# Revit family: 879-003X99-001-DN65-250
name_source: partatom
category: Pipe Accessories
units: mm (PartAtom-declared; Revit-internal decimal feet)

## family parameters
Always vertical = Yes
Cut with Voids When Loaded = No
Part Type = Valve - Breaks Into
Round Connector Dimension = Use Diameter
Shared = No
Work Plane-Based = No

## types (47) — shared parameters
879-0065-00-14400309999 = DN65_PN10/16
879-0065-00-14400319999 = DN65_PN10/16
879-0065-00-144003199A0 = DN65_PN10/16
879-0065-00-14400329999 = DN65_PN10/16
879-0065-00-14400339999 = DN65_PN10/16
879-0080-00-14400309999 = DN80_PN10/16
879-0080-00-14400319999 = DN80_PN10/16
879-0080-00-144003199A0 = DN80_PN10/16
879-0080-00-14400329999 = DN80_PN10/16
879-0080-00-14400339999 = DN80_PN10/16
879-0100-00-14400309999 = DN100_PN10/16
879-0100-00-14400319999 = DN100_PN10/16
879-0100-00-144003199A0 = DN100_PN10/16
879-0100-00-14400329999 = DN100_PN10/16
879-0100-00-14400339999 = DN100_PN10/16
879-0125-00-14400309999 = DN125_PN10/16
879-0125-00-14400319999 = DN125_PN10/16
879-0125-00-144003199A0 = DN125_PN10/16
879-0125-00-14400329999 = DN125_PN10/16
879-0125-00-14400339999 = DN125_PN10/16
879-0150-00-14400309999 = DN150_PN10/16
879-0150-00-14400319999 = DN150_PN10/16
879-0150-00-144003199A0 = DN150_PN10/16
879-0150-00-14400329999 = DN150_PN10/16
879-0150-00-14400339999 = DN150_PN10/16
879-0200-00-04400309999 = DN200_PN10
879-0200-00-04400319999 = DN200_PN10
879-0200-00-044003199A0 = DN200_PN10
879-0200-00-04400329999 = DN200_PN10
879-0200-00-04400339999 = DN200_PN10
879-0200-00-14400309999 = DN200_PN16
879-0200-00-14400319999 = DN200_PN16
879-0200-00-144003199A0 = DN200_PN16
879-0200-00-14400329999 = DN200_PN16
879-0200-00-14400339999 = DN200_PN16
879-0250-00-04400309999 = DN250_PN10
879-0250-00-04400319999 = DN250_PN10
879-0250-00-044003199A0 = DN250_PN10
879-0250-00-04400329999 = DN250_PN10
879-0250-00-04400339999 = DN250_PN10
879-0250-00-14400309999 = DN250_PN16
879-0250-00-14400319999 = DN250_PN16
879-0250-00-144003199A0 = DN250_PN16
879-0250-00-14400329999 = DN250_PN16
879-0250-00-14400339999 = DN250_PN16
Body_wall_thickness = 10 mm  [stored 0.0328084 ft]
Description_ = AVK ONE WAY ALTITUDE LEVEL CONTROL VALVE
Search_Table = 879-003X99-001-DN65-250
URL product pages = https://www.avkvalves.com

## per-type parameters (varying)
- 879-0065-00-14400309999_DN65_PN10/16: Body_Collar_Dia=26 mm; Body_Collar_Dia_2=18 mm  [stored 0.0590551 ft]; Body_Flange_Dia=83 mm; Body_Flange_Dia_2=91 mm; Body_Height_1=73 mm; Body_Height_2=36 mm; Body_Height_3=58 mm; Body_Height_4=51 mm; Body_Top_Dia=11 mm  [stored 0.0360892 ft]; Body_Top_Dia_2=9 mm  [stored 0.0295276 ft]; Body_With_Dia=36 mm; Body_With_Dia_1=73 mm; Body_With_Dia_2=73 mm; Bolt_support=223 mm; Bolt_support_2=112 mm; Bolt_support_Dia=12 mm  [stored 0.0393701 ft]; Bolt_support_lenght=53 mm; Bolt_support_lenght_2=63 mm; Bottom_profile=16 mm  [stored 0.0524934 ft]; D1=59 mm; D3=93 mm; DN=65 mm; Fillet_Length=6 mm  [stored 0.019685 ft]; Fillet_Length_Ref=18 mm  [stored 0.0590551 ft]; Flange_thickness=19 mm  [stored 0.062336 ft]; H=540 mm; H3_Ref=534 mm; ID=33 mm; L=290 mm; L_Ref=126 mm; NV_Dia=65 mm; PG_Dia=33 mm; PG_Ref=48 mm; PG_depth=8 mm  [stored 0.0262467 ft]; PG_height=232 mm; PG_height_1=216 mm; PG_ref=43 mm  [stored 0.141076 ft]; PR_1=71 mm; P_lenght=39 mm  [stored 0.127953 ft]; Pilot_Dia_1=18 mm  [stored 0.0590551 ft]; Pilot_Dia_2=35 mm  [stored 0.114829 ft]; Pilot_Dia_3=12 mm  [stored 0.0393701 ft]; Pilot_Dia_4=6 mm  [stored 0.019685 ft]; Pilot_Dia_5=4 mm  [stored 0.0131234 ft]; Pilot_top_1=312 mm; Pilot_top_ref=120 mm; Profile1_Height=117 mm; Profile1_Length=25 mm  [stored 0.082021 ft]; Profile1_Length_2=17 mm; Profile_Dia=6 mm  [stored 0.019685 ft]; Profile_Dia_2=6 mm  [stored 0.019685 ft]; Profile_Dia_3=12 mm  [stored 0.0393701 ft]; Profile_Dia_Ref=3 mm  [stored 0.00984252 ft]; Profile_Dia_Ref_2=12 mm  [stored 0.0393701 ft]; Profile_height ref=12 mm  [stored 0.0393701 ft]; T_Height=313 mm; T_Height_2=268 mm; T_Height_Ref_1=45 mm; T_Height_Ref_2=52 mm; T_ref=270 mm; Top_Profile=134 mm; Top_Profile_Ref=139 mm; W=540 mm; W_Ref=532 mm
- 879-0065-00-14400319999_DN65_PN10/16: Body_Collar_Dia=26 mm; Body_Collar_Dia_2=18 mm  [stored 0.0590551 ft]; Body_Flange_Dia=83 mm; Body_Flange_Dia_2=91 mm; Body_Height_1=73 mm; Body_Height_2=36 mm; Body_Height_3=58 mm; Body_Height_4=51 mm; Body_Top_Dia=11 mm  [stored 0.0360892 ft]; Body_Top_Dia_2=9 mm  [stored 0.0295276 ft]; Body_With_Dia=36 mm; Body_With_Dia_1=73 mm; Body_With_Dia_2=73 mm; Bolt_support=223 mm; Bolt_support_2=112 mm; Bolt_support_Dia=12 mm  [stored 0.0393701 ft]; Bolt_support_lenght=53 mm; Bolt_support_lenght_2=63 mm; Bottom_profile=16 mm  [stored 0.0524934 ft]; D1=59 mm; D3=93 mm; DN=65 mm; Fillet_Length=6 mm  [stored 0.019685 ft]; Fillet_Length_Ref=18 mm  [stored 0.0590551 ft]; Flange_thickness=19 mm  [stored 0.062336 ft]; H=540 mm; H3_Ref=534 mm; ID=33 mm; L=290 mm; L_Ref=126 mm; NV_Dia=65 mm; PG_Dia=33 mm; PG_Ref=48 mm; PG_depth=8 mm  [stored 0.0262467 ft]; PG_height=246 mm; PG_height_1=230 mm; PG_ref=43 mm  [stored 0.141076 ft]; PR_1=67 mm; P_lenght=39 mm  [stored 0.127953 ft]; Pilot_Dia_1=18 mm  [stored 0.0590551 ft]; Pilot_Dia_2=35 mm  [stored 0.114829 ft]; Pilot_Dia_3=12 mm  [stored 0.0393701 ft]; Pilot_Dia_4=6 mm  [stored 0.019685 ft]; Pilot_Dia_5=4 mm  [stored 0.0131234 ft]; Pilot_top_1=312 mm; Pilot_top_ref=120 mm; Profile1_Height=135 mm; Profile1_Length=25 mm  [stored 0.082021 ft]; Profile1_Length_2=17 mm; Profile_Dia=6 mm  [stored 0.019685 ft]; Profile_Dia_2=6 mm  [stored 0.019685 ft]; Profile_Dia_3=12 mm  [stored 0.0393701 ft]; Profile_Dia_Ref=3 mm  [stored 0.00984252 ft]; Profile_Dia_Ref_2=12 mm  [stored 0.0393701 ft]; Profile_height ref=12 mm  [stored 0.0393701 ft]; T_Height=295 mm; T_Height_2=252 mm; T_Height_Ref_1=42 mm; T_Height_Ref_2=49 mm; T_ref=280 mm; Top_Profile=134 mm; Top_Profile_Ref=139 mm; W=540 mm; W_Ref=532 mm
- 879-0065-00-144003199A0_DN65_PN10/16: Body_Collar_Dia=26 mm; Body_Collar_Dia_2=18 mm  [stored 0.0590551 ft]; Body_Flange_Dia=83 mm; Body_Flange_Dia_2=91 mm; Body_Height_1=73 mm; Body_Height_2=36 mm; Body_Height_3=58 mm; Body_Height_4=51 mm; Body_Top_Dia=11 mm  [stored 0.0360892 ft]; Body_Top_Dia_2=9 mm  [stored 0.0295276 ft]; Body_With_Dia=36 mm; Body_With_Dia_1=73 mm; Body_With_Dia_2=73 mm; Bolt_support=223 mm; Bolt_support_2=112 mm; Bolt_support_Dia=12 mm  [stored 0.0393701 ft]; Bolt_support_lenght=53 mm; Bolt_support_lenght_2=63 mm; Bottom_profile=16 mm  [stored 0.0524934 ft]; D1=59 mm; D3=93 mm; DN=65 mm; Fillet_Length=6 mm  [stored 0.019685 ft]; Fillet_Length_Ref=18 mm  [stored 0.0590551 ft]; Flange_thickness=19 mm  [stored 0.062336 ft]; H=540 mm; H3_Ref=534 mm; ID=33 mm; L=290 mm; L_Ref=126 mm; NV_Dia=65 mm; PG_Dia=33 mm; PG_Ref=48 mm; PG_depth=8 mm  [stored 0.0262467 ft]; PG_height=232 mm; PG_height_1=216 mm; PG_ref=43 mm  [stored 0.141076 ft]; PR_1=71 mm; P_lenght=39 mm  [stored 0.127953 ft]; Pilot_Dia_1=18 mm  [stored 0.0590551 ft]; Pilot_Dia_2=35 mm  [stored 0.114829 ft]; Pilot_Dia_3=12 mm  [stored 0.0393701 ft]; Pilot_Dia_4=6 mm  [stored 0.019685 ft]; Pilot_Dia_5=4 mm  [stored 0.0131234 ft]; Pilot_top_1=312 mm; Pilot_top_ref=120 mm; Profile1_Height=117 mm; Profile1_Length=25 mm  [stored 0.082021 ft]; Profile1_Length_2=17 mm; Profile_Dia=6 mm  [stored 0.019685 ft]; Profile_Dia_2=6 mm  [stored 0.019685 ft]; Profile_Dia_3=12 mm  [stored 0.0393701 ft]; Profile_Dia_Ref=3 mm  [stored 0.00984252 ft]; Profile_Dia_Ref_2=12 mm  [stored 0.0393701 ft]; Profile_height ref=12 mm  [stored 0.0393701 ft]; T_Height=313 mm; T_Height_2=268 mm; T_Height_Ref_1=45 mm; T_Height_Ref_2=52 mm; T_ref=270 mm; Top_Profile=134 mm; Top_Profile_Ref=139 mm; W=540 mm; W_Ref=532 mm
- 879-0065-00-14400329999_DN65_PN10/16: Body_Collar_Dia=26 mm; Body_Collar_Dia_2=18 mm  [stored 0.0590551 ft]; Body_Flange_Dia=83 mm; Body_Flange_Dia_2=91 mm; Body_Height_1=73 mm; Body_Height_2=36 mm; Body_Height_3=73 mm; Body_Height_4=51 mm; Body_Top_Dia=11 mm  [stored 0.0360892 ft]; Body_Top_Dia_2=9 mm  [stored 0.0295276 ft]; Body_With_Dia=36 mm; Body_With_Dia_1=73 mm; Body_With_Dia_2=73 mm; Bolt_support=223 mm; Bolt_support_2=112 mm; Bolt_support_Dia=12 mm  [stored 0.0393701 ft]; Bolt_support_lenght=53 mm; Bolt_support_lenght_2=63 mm; Bottom_profile=16 mm  [stored 0.0524934 ft]; D1=59 mm; D3=93 mm; DN=65 mm; Fillet_Length=6 mm  [stored 0.019685 ft]; Fillet_Length_Ref=18 mm  [stored 0.0590551 ft]; Flange_thickness=19 mm  [stored 0.062336 ft]; H=540 mm; H3_Ref=534 mm; ID=33 mm; L=290 mm; L_Ref=126 mm; NV_Dia=65 mm; PG_Dia=33 mm; PG_Ref=48 mm; PG_depth=8 mm  [stored 0.0262467 ft]; PG_height=246 mm; PG_height_1=230 mm; PG_ref=43 mm  [stored 0.141076 ft]; PR_1=67 mm; P_lenght=39 mm  [stored 0.127953 ft]; Pilot_Dia_1=18 mm  [stored 0.0590551 ft]; Pilot_Dia_2=35 mm  [stored 0.114829 ft]; Pilot_Dia_3=12 mm  [stored 0.0393701 ft]; Pilot_Dia_4=6 mm  [stored 0.019685 ft]; Pilot_Dia_5=4 mm  [stored 0.0131234 ft]; Pilot_top_1=319 mm; Pilot_top_ref=113 mm; Profile1_Height=135 mm; Profile1_Length=25 mm  [stored 0.082021 ft]; Profile1_Length_2=17 mm; Profile_Dia=6 mm  [stored 0.019685 ft]; Profile_Dia_2=6 mm  [stored 0.019685 ft]; Profile_Dia_3=12 mm  [stored 0.0393701 ft]; Profile_Dia_Ref=3 mm  [stored 0.00984252 ft]; Profile_Dia_Ref_2=12 mm  [stored 0.0393701 ft]; Profile_height ref=12 mm  [stored 0.0393701 ft]; T_Height=295 mm; T_Height_2=252 mm; T_Height_Ref_1=42 mm; T_Height_Ref_2=49 mm; T_ref=280 mm; Top_Profile=134 mm; Top_Profile_Ref=139 mm; W=540 mm; W_Ref=532 mm
- 879-0065-00-14400339999_DN65_PN10/16: Body_Collar_Dia=26 mm; Body_Collar_Dia_2=18 mm  [stored 0.0590551 ft]; Body_Flange_Dia=83 mm; Body_Flange_Dia_2=91 mm; Body_Height_1=73 mm; Body_Height_2=36 mm; Body_Height_3=58 mm; Body_Height_4=51 mm; Body_Top_Dia=11 mm  [stored 0.0360892 ft]; Body_Top_Dia_2=9 mm  [stored 0.0295276 ft]; Body_With_Dia=36 mm; Body_With_Dia_1=73 mm; Body_With_Dia_2=73 mm; Bolt_support=223 mm; Bolt_support_2=112 mm; Bolt_support_Dia=12 mm  [stored 0.0393701 ft]; Bolt_support_lenght=53 mm; Bolt_support_lenght_2=63 mm; Bottom_profile=16 mm  [stored 0.0524934 ft]; D1=59 mm; D3=93 mm; DN=65 mm; Fillet_Length=6 mm  [stored 0.019685 ft]; Fillet_Length_Ref=18 mm  [stored 0.0590551 ft]; Flange_thickness=19 mm  [stored 0.062336 ft]; H=540 mm; H3_Ref=534 mm; ID=33 mm; L=290 mm; L_Ref=126 mm; NV_Dia=65 mm; PG_Dia=33 mm; PG_Ref=48 mm; PG_depth=8 mm  [stored 0.0262467 ft]; PG_height=232 mm; PG_height_1=216 mm; PG_ref=43 mm  [stored 0.141076 ft]; PR_1=71 mm; P_lenght=39 mm  [stored 0.127953 ft]; Pilot_Dia_1=18 mm  [stored 0.0590551 ft]; Pilot_Dia_2=35 mm  [stored 0.114829 ft]; Pilot_Dia_3=12 mm  [stored 0.0393701 ft]; Pilot_Dia_4=6 mm  [stored 0.019685 ft]; Pilot_Dia_5=4 mm  [stored 0.0131234 ft]; Pilot_top_1=312 mm; Pilot_top_ref=120 mm; Profile1_Height=117 mm; Profile1_Length=25 mm  [stored 0.082021 ft]; Profile1_Length_2=17 mm; Profile_Dia=6 mm  [stored 0.019685 ft]; Profile_Dia_2=6 mm  [stored 0.019685 ft]; Profile_Dia_3=12 mm  [stored 0.0393701 ft]; Profile_Dia_Ref=3 mm  [stored 0.00984252 ft]; Profile_Dia_Ref_2=12 mm  [stored 0.0393701 ft]; Profile_height ref=12 mm  [stored 0.0393701 ft]; T_Height=313 mm; T_Height_2=268 mm; T_Height_Ref_1=45 mm; T_Height_Ref_2=52 mm; T_ref=270 mm; Top_Profile=134 mm; Top_Profile_Ref=139 mm; W=540 mm; W_Ref=532 mm
- 879-0080-00-14400309999_DN80_PN10/16: Body_Collar_Dia=28 mm; Body_Collar_Dia_2=19 mm  [stored 0.062336 ft]; Body_Flange_Dia=89 mm; Body_Flange_Dia_2=97 mm; Body_Height_1=78 mm; Body_Height_2=39 mm  [stored 0.127953 ft]; Body_Height_3=62 mm; Body_Height_4=54 mm; Body_Top_Dia=11 mm  [stored 0.0360892 ft]; Body_Top_Dia_2=10 mm  [stored 0.0328084 ft]; Body_With_Dia=39 mm  [stored 0.127953 ft]; Body_With_Dia_1=78 mm; Body_With_Dia_2=78 mm; Bolt_support=238 mm; Bolt_support_2=119 mm; Bolt_support_Dia=12 mm  [stored 0.0393701 ft]; Bolt_support_lenght=60 mm; Bolt_support_lenght_2=70 mm; Bottom_profile=20 mm  [stored 0.0656168 ft]; D1=66 mm; D3=100 mm; DN=80 mm; Fillet_Length=6 mm  [stored 0.019685 ft]; Fillet_Length_Ref=18 mm  [stored 0.0590551 ft]; Flange_thickness=19 mm  [stored 0.062336 ft]; H=555 mm; H3_Ref=549 mm; ID=40 mm  [stored 0.131234 ft]; L=310 mm; L_Ref=136 mm; NV_Dia=80 mm; PG_Dia=40 mm  [stored 0.131234 ft]; PG_Ref=52 mm; PG_depth=8 mm  [stored 0.0262467 ft]; PG_height=262 mm; PG_height_1=242 mm; PG_ref=50 mm; PR_1=66 mm; P_lenght=43 mm  [stored 0.141076 ft]; Pilot_Dia_1=20 mm  [stored 0.0656168 ft]; Pilot_Dia_2=39 mm  [stored 0.127953 ft]; Pilot_Dia_3=13 mm; Pilot_Dia_4=7 mm  [stored 0.0229659 ft]; Pilot_Dia_5=4 mm  [stored 0.0131234 ft]; Pilot_top_1=321 mm; Pilot_top_ref=118 mm; Profile1_Height=144 mm; Profile1_Length=27 mm  [stored 0.0885827 ft]; Profile1_Length_2=18 mm  [stored 0.0590551 ft]; Profile_Dia=6 mm  [stored 0.019685 ft]; Profile_Dia_2=6 mm  [stored 0.019685 ft]; Profile_Dia_3=12 mm  [stored 0.0393701 ft]; Profile_Dia_Ref=3 mm  [stored 0.00984252 ft]; Profile_Dia_Ref_2=12 mm  [stored 0.0393701 ft]; Profile_height ref=12 mm  [stored 0.0393701 ft]; T_Height=293 mm; T_Height_2=251 mm; T_Height_Ref_1=42 mm; T_Height_Ref_2=49 mm; T_ref=289 mm; Top_Profile=143 mm; Top_Profile_Ref=148 mm; W=560 mm; W_Ref=552 mm
- 879-0080-00-144003099A0_DN80_PN10/16: Body_Collar_Dia=28 mm; Body_Collar_Dia_2=19 mm  [stored 0.062336 ft]; Body_Flange_Dia=89 mm; Body_Flange_Dia_2=97 mm; Body_Height_1=78 mm; Body_Height_2=39 mm  [stored 0.127953 ft]; Body_Height_3=62 mm; Body_Height_4=54 mm; Body_Top_Dia=11 mm  [stored 0.0360892 ft]; Body_Top_Dia_2=10 mm  [stored 0.0328084 ft]; Body_With_Dia=39 mm  [stored 0.127953 ft]; Body_With_Dia_1=78 mm; Body_With_Dia_2=78 mm; Bolt_support=238 mm; Bolt_support_2=119 mm; Bolt_support_Dia=12 mm  [stored 0.0393701 ft]; Bolt_support_lenght=60 mm; Bolt_support_lenght_2=70 mm; Bottom_profile=20 mm  [stored 0.0656168 ft]; D1=66 mm; D3=100 mm; DN=80 mm; Fillet_Length=6 mm  [stored 0.019685 ft]; Fillet_Length_Ref=18 mm  [stored 0.0590551 ft]; Flange_thickness=19 mm  [stored 0.062336 ft]; H=555 mm; H3_Ref=549 mm; ID=40 mm  [stored 0.131234 ft]; L=310 mm; L_Ref=136 mm; NV_Dia=80 mm; PG_Dia=40 mm  [stored 0.131234 ft]; PG_Ref=52 mm; PG_depth=8 mm  [stored 0.0262467 ft]; PG_height=254 mm; PG_height_1=234 mm; PG_ref=50 mm; PR_1=69 mm; P_lenght=43 mm  [stored 0.141076 ft]; Pilot_Dia_1=20 mm  [stored 0.0656168 ft]; Pilot_Dia_2=39 mm  [stored 0.127953 ft]; Pilot_Dia_3=13 mm; Pilot_Dia_4=7 mm  [stored 0.0229659 ft]; Pilot_Dia_5=4 mm  [stored 0.0131234 ft]; Pilot_top_1=321 mm; Pilot_top_ref=118 mm; Profile1_Height=133 mm; Profile1_Length=27 mm  [stored 0.0885827 ft]; Profile1_Length_2=18 mm  [stored 0.0590551 ft]; Profile_Dia=6 mm  [stored 0.019685 ft]; Profile_Dia_2=6 mm  [stored 0.019685 ft]; Profile_Dia_3=12 mm  [stored 0.0393701 ft]; Profile_Dia_Ref=3 mm  [stored 0.00984252 ft]; Profile_Dia_Ref_2=12 mm  [stored 0.0393701 ft]; Profile_height ref=12 mm  [stored 0.0393701 ft]; T_Height=304 mm; T_Height_2=261 mm; T_Height_Ref_1=43 mm  [stored 0.141076 ft]; T_Height_Ref_2=51 mm; T_ref=283 mm; Top_Profile=143 mm; Top_Profile_Ref=148 mm; W=560 mm; W_Ref=552 mm
- 879-0080-00-14400319999_DN80_PN10/16: Body_Collar_Dia=28 mm; Body_Collar_Dia_2=19 mm  [stored 0.062336 ft]; Body_Flange_Dia=89 mm; Body_Flange_Dia_2=97 mm; Body_Height_1=78 mm; Body_Height_2=39 mm  [stored 0.127953 ft]; Body_Height_3=62 mm; Body_Height_4=54 mm; Body_Top_Dia=11 mm  [stored 0.0360892 ft]; Body_Top_Dia_2=10 mm  [stored 0.0328084 ft]; Body_With_Dia=39 mm  [stored 0.127953 ft]; Body_With_Dia_1=78 mm; Body_With_Dia_2=78 mm; Bolt_support=238 mm; Bolt_support_2=119 mm; Bolt_support_Dia=12 mm  [stored 0.0393701 ft]; Bolt_support_lenght=60 mm; Bolt_support_lenght_2=70 mm; Bottom_profile=20 mm  [stored 0.0656168 ft]; D1=66 mm; D3=100 mm; DN=80 mm; Fillet_Length=6 mm  [stored 0.019685 ft]; Fillet_Length_Ref=18 mm  [stored 0.0590551 ft]; Flange_thickness=19 mm  [stored 0.062336 ft]; H=555 mm; H3_Ref=549 mm; ID=40 mm  [stored 0.131234 ft]; L=310 mm; L_Ref=136 mm; NV_Dia=80 mm; PG_Dia=40 mm  [stored 0.131234 ft]; PG_Ref=52 mm; PG_depth=8 mm  [stored 0.0262467 ft]; PG_height=262 mm; PG_height_1=242 mm; PG_ref=50 mm; PR_1=66 mm; P_lenght=43 mm  [stored 0.141076 ft]; Pilot_Dia_1=20 mm  [stored 0.0656168 ft]; Pilot_Dia_2=39 mm  [stored 0.127953 ft]; Pilot_Dia_3=13 mm; Pilot_Dia_4=7 mm  [stored 0.0229659 ft]; Pilot_Dia_5=4 mm  [stored 0.0131234 ft]; Pilot_top_1=321 mm; Pilot_top_ref=118 mm; Profile1_Height=144 mm; Profile1_Length=27 mm  [stored 0.0885827 ft]; Profile1_Length_2=18 mm  [stored 0.0590551 ft]; Profile_Dia=6 mm  [stored 0.019685 ft]; Profile_Dia_2=6 mm  [stored 0.019685 ft]; Profile_Dia_3=12 mm  [stored 0.0393701 ft]; Profile_Dia_Ref=3 mm  [stored 0.00984252 ft]; Profile_Dia_Ref_2=12 mm  [stored 0.0393701 ft]; Profile_height ref=12 mm  [stored 0.0393701 ft]; T_Height=293 mm; T_Height_2=251 mm; T_Height_Ref_1=42 mm; T_Height_Ref_2=49 mm; T_ref=289 mm; Top_Profile=143 mm; Top_Profile_Ref=148 mm; W=560 mm; W_Ref=552 mm
- 879-0080-00-144003199A0_DN80_PN10/16: Body_Collar_Dia=28 mm; Body_Collar_Dia_2=19 mm  [stored 0.062336 ft]; Body_Flange_Dia=89 mm; Body_Flange_Dia_2=97 mm; Body_Height_1=78 mm; Body_Height_2=39 mm  [stored 0.127953 ft]; Body_Height_3=78 mm; Body_Height_4=54 mm; Body_Top_Dia=11 mm  [stored 0.0360892 ft]; Body_Top_Dia_2=10 mm  [stored 0.0328084 ft]; Body_With_Dia=39 mm  [stored 0.127953 ft]; Body_With_Dia_1=78 mm; Body_With_Dia_2=78 mm; Bolt_support=238 mm; Bolt_support_2=119 mm; Bolt_support_Dia=12 mm  [stored 0.0393701 ft]; Bolt_support_lenght=60 mm; Bolt_support_lenght_2=70 mm; Bottom_profile=20 mm  [stored 0.0656168 ft]; D1=66 mm; D3=100 mm; DN=80 mm; Fillet_Length=6 mm  [stored 0.019685 ft]; Fillet_Length_Ref=18 mm  [stored 0.0590551 ft]; Flange_thickness=19 mm  [stored 0.062336 ft]; H=555 mm; H3_Ref=549 mm; ID=40 mm  [stored 0.131234 ft]; L=310 mm; L_Ref=136 mm; NV_Dia=80 mm; PG_Dia=40 mm  [stored 0.131234 ft]; PG_Ref=52 mm; PG_depth=8 mm  [stored 0.0262467 ft]; PG_height=254 mm; PG_height_1=234 mm; PG_ref=50 mm; PR_1=69 mm; P_lenght=43 mm  [stored 0.141076 ft]; Pilot_Dia_1=20 mm  [stored 0.0656168 ft]; Pilot_Dia_2=39 mm  [stored 0.127953 ft]; Pilot_Dia_3=13 mm; Pilot_Dia_4=7 mm  [stored 0.0229659 ft]; Pilot_Dia_5=4 mm  [stored 0.0131234 ft]; Pilot_top_1=329 mm; Pilot_top_ref=110 mm; Profile1_Height=133 mm; Profile1_Length=27 mm  [stored 0.0885827 ft]; Profile1_Length_2=18 mm  [stored 0.0590551 ft]; Profile_Dia=6 mm  [stored 0.019685 ft]; Profile_Dia_2=6 mm  [stored 0.019685 ft]; Profile_Dia_3=12 mm  [stored 0.0393701 ft]; Profile_Dia_Ref=3 mm  [stored 0.00984252 ft]; Profile_Dia_Ref_2=12 mm  [stored 0.0393701 ft]; Profile_height ref=12 mm  [stored 0.0393701 ft]; T_Height=304 mm; T_Height_2=261 mm; T_Height_Ref_1=43 mm  [stored 0.141076 ft]; T_Height_Ref_2=51 mm; T_ref=283 mm; Top_Profile=143 mm; Top_Profile_Ref=148 mm; W=560 mm; W_Ref=552 mm
- 879-0080-00-14400329999_DN80_PN10/16: Body_Collar_Dia=28 mm; Body_Collar_Dia_2=19 mm  [stored 0.062336 ft]; Body_Flange_Dia=89 mm; Body_Flange_Dia_2=97 mm; Body_Height_1=78 mm; Body_Height_2=39 mm  [stored 0.127953 ft]; Body_Height_3=62 mm; Body_Height_4=54 mm; Body_Top_Dia=11 mm  [stored 0.0360892 ft]; Body_Top_Dia_2=10 mm  [stored 0.0328084 ft]; Body_With_Dia=39 mm  [stored 0.127953 ft]; Body_With_Dia_1=78 mm; Body_With_Dia_2=78 mm; Bolt_support=238 mm; Bolt_support_2=119 mm; Bolt_support_Dia=12 mm  [stored 0.0393701 ft]; Bolt_support_lenght=60 mm; Bolt_support_lenght_2=70 mm; Bottom_profile=20 mm  [stored 0.0656168 ft]; D1=66 mm; D3=100 mm; DN=80 mm; Fillet_Length=6 mm  [stored 0.019685 ft]; Fillet_Length_Ref=18 mm  [stored 0.0590551 ft]; Flange_thickness=19 mm  [stored 0.062336 ft]; H=555 mm; H3_Ref=549 mm; ID=40 mm  [stored 0.131234 ft]; L=310 mm; L_Ref=136 mm; NV_Dia=80 mm; PG_Dia=40 mm  [stored 0.131234 ft]; PG_Ref=52 mm; PG_depth=8 mm  [stored 0.0262467 ft]; PG_height=262 mm; PG_height_1=242 mm; PG_ref=50 mm; PR_1=66 mm; P_lenght=43 mm  [stored 0.141076 ft]; Pilot_Dia_1=20 mm  [stored 0.0656168 ft]; Pilot_Dia_2=39 mm  [stored 0.127953 ft]; Pilot_Dia_3=13 mm; Pilot_Dia_4=7 mm  [stored 0.0229659 ft]; Pilot_Dia_5=4 mm  [stored 0.0131234 ft]; Pilot_top_1=321 mm; Pilot_top_ref=118 mm; Profile1_Height=144 mm; Profile1_Length=27 mm  [stored 0.0885827 ft]; Profile1_Length_2=18 mm  [stored 0.0590551 ft]; Profile_Dia=6 mm  [stored 0.019685 ft]; Profile_Dia_2=6 mm  [stored 0.019685 ft]; Profile_Dia_3=12 mm  [stored 0.0393701 ft]; Profile_Dia_Ref=3 mm  [stored 0.00984252 ft]; Profile_Dia_Ref_2=12 mm  [stored 0.0393701 ft]; Profile_height ref=12 mm  [stored 0.0393701 ft]; T_Height=293 mm; T_Height_2=251 mm; T_Height_Ref_1=42 mm; T_Height_Ref_2=49 mm; T_ref=289 mm; Top_Profile=143 mm; Top_Profile_Ref=148 mm; W=560 mm; W_Ref=552 mm
- 879-0080-00-14400339999_DN80_PN10/16: Body_Collar_Dia=28 mm; Body_Collar_Dia_2=19 mm  [stored 0.062336 ft]; Body_Flange_Dia=89 mm; Body_Flange_Dia_2=97 mm; Body_Height_1=78 mm; Body_Height_2=39 mm  [stored 0.127953 ft]; Body_Height_3=78 mm; Body_Height_4=54 mm; Body_Top_Dia=11 mm  [stored 0.0360892 ft]; Body_Top_Dia_2=10 mm  [stored 0.0328084 ft]; Body_With_Dia=39 mm  [stored 0.127953 ft]; Body_With_Dia_1=78 mm; Body_With_Dia_2=78 mm; Bolt_support=238 mm; Bolt_support_2=119 mm; Bolt_support_Dia=12 mm  [stored 0.0393701 ft]; Bolt_support_lenght=60 mm; Bolt_support_lenght_2=70 mm; Bottom_profile=20 mm  [stored 0.0656168 ft]; D1=66 mm; D3=100 mm; DN=81 mm; Fillet_Length=6 mm  [stored 0.019685 ft]; Fillet_Length_Ref=18 mm  [stored 0.0590551 ft]; Flange_thickness=19 mm  [stored 0.062336 ft]; H=555 mm; H3_Ref=549 mm; ID=40 mm  [stored 0.131234 ft]; L=310 mm; L_Ref=136 mm; NV_Dia=80 mm; PG_Dia=40 mm  [stored 0.131234 ft]; PG_Ref=52 mm; PG_depth=8 mm  [stored 0.0262467 ft]; PG_height=254 mm; PG_height_1=234 mm; PG_ref=50 mm; PR_1=69 mm; P_lenght=43 mm  [stored 0.141076 ft]; Pilot_Dia_1=20 mm  [stored 0.0656168 ft]; Pilot_Dia_2=39 mm  [stored 0.127953 ft]; Pilot_Dia_3=13 mm; Pilot_Dia_4=7 mm  [stored 0.0229659 ft]; Pilot_Dia_5=4 mm  [stored 0.0131234 ft]; Pilot_top_1=329 mm; Pilot_top_ref=110 mm; Profile1_Height=133 mm; Profile1_Length=27 mm  [stored 0.0885827 ft]; Profile1_Length_2=18 mm  [stored 0.0590551 ft]; Profile_Dia=6 mm  [stored 0.019685 ft]; Profile_Dia_2=6 mm  [stored 0.019685 ft]; Profile_Dia_3=12 mm  [stored 0.0393701 ft]; Profile_Dia_Ref=3 mm  [stored 0.00984252 ft]; Profile_Dia_Ref_2=12 mm  [stored 0.0393701 ft]; Profile_height ref=12 mm  [stored 0.0393701 ft]; T_Height=304 mm; T_Height_2=261 mm; T_Height_Ref_1=43 mm  [stored 0.141076 ft]; T_Height_Ref_2=51 mm; T_ref=283 mm; Top_Profile=143 mm; Top_Profile_Ref=148 mm; W=560 mm; W_Ref=552 mm
- 879-0100-00-14400309999_DN100_PN10/16: Body_Collar_Dia=32 mm  [stored 0.104987 ft]; Body_Collar_Dia_2=22 mm  [stored 0.0721785 ft]; Body_Flange_Dia=100 mm; Body_Flange_Dia_2=109 mm; Body_Height_1=88 mm; Body_Height_2=44 mm; Body_Height_3=59 mm; Body_Height_4=59 mm; Body_Top_Dia=13 mm; Body_Top_Dia_2=11 mm  [stored 0.0360892 ft]; Body_With_Dia=44 mm; Body_With_Dia_1=88 mm; Body_With_Dia_2=88 mm; Bolt_support=269 mm; Bolt_support_2=135 mm; Bolt_support_Dia=12 mm  [stored 0.0393701 ft]; Bolt_support_lenght=70 mm; Bolt_support_lenght_2=80 mm; Bottom_profile=25 mm  [stored 0.082021 ft]; D1=78 mm; D3=110 mm; DN=100 mm; Fillet_Length=6 mm  [stored 0.019685 ft]; Fillet_Length_Ref=18 mm  [stored 0.0590551 ft]; Flange_thickness=19 mm  [stored 0.062336 ft]; H=570 mm; H3_Ref=564 mm; ID=50 mm; L=350 mm; L_Ref=156 mm; NV_Dia=100 mm; PG_Dia=50 mm; PG_Ref=58 mm; PG_depth=8 mm  [stored 0.0262467 ft]; PG_height=278 mm; PG_height_1=253 mm; PG_ref=60 mm; PR_1=66 mm; P_lenght=48 mm; Pilot_Dia_1=22 mm  [stored 0.0721785 ft]; Pilot_Dia_2=44 mm; Pilot_Dia_3=15 mm  [stored 0.0492126 ft]; Pilot_Dia_4=7 mm  [stored 0.0229659 ft]; Pilot_Dia_5=5 mm  [stored 0.0164042 ft]; Pilot_top_1=329 mm; Pilot_top_ref=115 mm; Profile1_Height=150 mm; Profile1_Length=30 mm  [stored 0.0984252 ft]; Profile1_Length_2=20 mm  [stored 0.0656168 ft]; Profile_Dia=6 mm  [stored 0.019685 ft]; Profile_Dia_2=6 mm  [stored 0.019685 ft]; Profile_Dia_3=12 mm  [stored 0.0393701 ft]; Profile_Dia_Ref=3 mm  [stored 0.00984252 ft]; Profile_Dia_Ref_2=12 mm  [stored 0.0393701 ft]; Profile_height ref=12 mm  [stored 0.0393701 ft]; T_Height=292 mm; T_Height_2=250 mm; T_Height_Ref_1=42 mm; T_Height_Ref_2=49 mm; T_ref=294 mm; Top_Profile=162 mm; Top_Profile_Ref=167 mm; W=575 mm; W_Ref=567 mm
- 879-0100-00-144003099A0_DN100_PN10/16: Body_Collar_Dia=32 mm  [stored 0.104987 ft]; Body_Collar_Dia_2=22 mm  [stored 0.0721785 ft]; Body_Flange_Dia=100 mm; Body_Flange_Dia_2=109 mm; Body_Height_1=88 mm; Body_Height_2=44 mm; Body_Height_3=59 mm; Body_Height_4=59 mm; Body_Top_Dia=13 mm; Body_Top_Dia_2=11 mm  [stored 0.0360892 ft]; Body_With_Dia=44 mm; Body_With_Dia_1=88 mm; Body_With_Dia_2=88 mm; Bolt_support=269 mm; Bolt_support_2=135 mm; Bolt_support_Dia=12 mm  [stored 0.0393701 ft]; Bolt_support_lenght=70 mm; Bolt_support_lenght_2=80 mm; Bottom_profile=25 mm  [stored 0.082021 ft]; D1=78 mm; D3=110 mm; DN=100 mm; Fillet_Length=6 mm  [stored 0.019685 ft]; Fillet_Length_Ref=18 mm  [stored 0.0590551 ft]; Flange_thickness=19 mm  [stored 0.062336 ft]; H=570 mm; H3_Ref=564 mm; ID=50 mm; L=350 mm; L_Ref=156 mm; NV_Dia=100 mm; PG_Dia=50 mm; PG_Ref=58 mm; PG_depth=8 mm  [stored 0.0262467 ft]; PG_height=271 mm; PG_height_1=246 mm; PG_ref=60 mm; PR_1=68 mm; P_lenght=48 mm; Pilot_Dia_1=22 mm  [stored 0.0721785 ft]; Pilot_Dia_2=44 mm; Pilot_Dia_3=15 mm  [stored 0.0492126 ft]; Pilot_Dia_4=7 mm  [stored 0.0229659 ft]; Pilot_Dia_5=5 mm  [stored 0.0164042 ft]; Pilot_top_1=329 mm; Pilot_top_ref=115 mm; Profile1_Height=141 mm; Profile1_Length=30 mm  [stored 0.0984252 ft]; Profile1_Length_2=20 mm  [stored 0.0656168 ft]; Profile_Dia=6 mm  [stored 0.019685 ft]; Profile_Dia_2=6 mm  [stored 0.019685 ft]; Profile_Dia_3=12 mm  [stored 0.0393701 ft]; Profile_Dia_Ref=3 mm  [stored 0.00984252 ft]; Profile_Dia_Ref_2=12 mm  [stored 0.0393701 ft]; Profile_height ref=12 mm  [stored 0.0393701 ft]; T_Height=301 mm; T_Height_2=258 mm; T_Height_Ref_1=43 mm  [stored 0.141076 ft]; T_Height_Ref_2=50 mm; T_ref=289 mm; Top_Profile=162 mm; Top_Profile_Ref=167 mm; W=575 mm; W_Ref=567 mm
- 879-0100-00-14400319999_DN100_PN10/16: Body_Collar_Dia=32 mm  [stored 0.104987 ft]; Body_Collar_Dia_2=22 mm  [stored 0.0721785 ft]; Body_Flange_Dia=100 mm; Body_Flange_Dia_2=109 mm; Body_Height_1=88 mm; Body_Height_2=44 mm; Body_Height_3=59 mm; Body_Height_4=59 mm; Body_Top_Dia=13 mm; Body_Top_Dia_2=11 mm  [stored 0.0360892 ft]; Body_With_Dia=44 mm; Body_With_Dia_1=88 mm; Body_With_Dia_2=88 mm; Bolt_support=269 mm; Bolt_support_2=135 mm; Bolt_support_Dia=12 mm  [stored 0.0393701 ft]; Bolt_support_lenght=70 mm; Bolt_support_lenght_2=80 mm; Bottom_profile=25 mm  [stored 0.082021 ft]; D1=78 mm; D3=110 mm; DN=100 mm; Fillet_Length=6 mm  [stored 0.019685 ft]; Fillet_Length_Ref=18 mm  [stored 0.0590551 ft]; Flange_thickness=19 mm  [stored 0.062336 ft]; H=570 mm; H3_Ref=564 mm; ID=50 mm; L=350 mm; L_Ref=156 mm; NV_Dia=100 mm; PG_Dia=50 mm; PG_Ref=58 mm; PG_depth=8 mm  [stored 0.0262467 ft]; PG_height=278 mm; PG_height_1=253 mm; PG_ref=60 mm; PR_1=66 mm; P_lenght=48 mm; Pilot_Dia_1=22 mm  [stored 0.0721785 ft]; Pilot_Dia_2=44 mm; Pilot_Dia_3=15 mm  [stored 0.0492126 ft]; Pilot_Dia_4=7 mm  [stored 0.0229659 ft]; Pilot_Dia_5=5 mm  [stored 0.0164042 ft]; Pilot_top_1=329 mm; Pilot_top_ref=115 mm; Profile1_Height=150 mm; Profile1_Length=30 mm  [stored 0.0984252 ft]; Profile1_Length_2=20 mm  [stored 0.0656168 ft]; Profile_Dia=6 mm  [stored 0.019685 ft]; Profile_Dia_2=6 mm  [stored 0.019685 ft]; Profile_Dia_3=12 mm  [stored 0.0393701 ft]; Profile_Dia_Ref=3 mm  [stored 0.00984252 ft]; Profile_Dia_Ref_2=12 mm  [stored 0.0393701 ft]; Profile_height ref=12 mm  [stored 0.0393701 ft]; T_Height=292 mm; T_Height_2=250 mm; T_Height_Ref_1=42 mm; T_Height_Ref_2=49 mm; T_ref=294 mm; Top_Profile=162 mm; Top_Profile_Ref=167 mm; W=575 mm; W_Ref=567 mm
- 879-0100-00-144003199A0_DN100_PN10/16: Body_Collar_Dia=32 mm  [stored 0.104987 ft]; Body_Collar_Dia_2=22 mm  [stored 0.0721785 ft]; Body_Flange_Dia=100 mm; Body_Flange_Dia_2=109 mm; Body_Height_1=88 mm; Body_Height_2=44 mm; Body_Height_3=70 mm; Body_Height_4=59 mm; Body_Top_Dia=13 mm; Body_Top_Dia_2=11 mm  [stored 0.0360892 ft]; Body_With_Dia=44 mm; Body_With_Dia_1=88 mm; Body_With_Dia_2=88 mm; Bolt_support=269 mm; Bolt_support_2=135 mm; Bolt_support_Dia=12 mm  [stored 0.0393701 ft]; Bolt_support_lenght=70 mm; Bolt_support_lenght_2=80 mm; Bottom_profile=25 mm  [stored 0.082021 ft]; D1=78 mm; D3=110 mm; DN=100 mm; Fillet_Length=6 mm  [stored 0.019685 ft]; Fillet_Length_Ref=18 mm  [stored 0.0590551 ft]; Flange_thickness=19 mm  [stored 0.062336 ft]; H=570 mm; H3_Ref=564 mm; ID=50 mm; L=350 mm; L_Ref=156 mm; NV_Dia=100 mm; PG_Dia=50 mm; PG_Ref=58 mm; PG_depth=8 mm  [stored 0.0262467 ft]; PG_height=271 mm; PG_height_1=246 mm; PG_ref=60 mm; PR_1=68 mm; P_lenght=48 mm; Pilot_Dia_1=22 mm  [stored 0.0721785 ft]; Pilot_Dia_2=44 mm; Pilot_Dia_3=15 mm  [stored 0.0492126 ft]; Pilot_Dia_4=7 mm  [stored 0.0229659 ft]; Pilot_Dia_5=5 mm  [stored 0.0164042 ft]; Pilot_top_1=335 mm; Pilot_top_ref=109 mm; Profile1_Height=141 mm; Profile1_Length=30 mm  [stored 0.0984252 ft]; Profile1_Length_2=20 mm  [stored 0.0656168 ft]; Profile_Dia=6 mm  [stored 0.019685 ft]; Profile_Dia_2=6 mm  [stored 0.019685 ft]; Profile_Dia_3=12 mm  [stored 0.0393701 ft]; Profile_Dia_Ref=3 mm  [stored 0.00984252 ft]; Profile_Dia_Ref_2=12 mm  [stored 0.0393701 ft]; Profile_height ref=12 mm  [stored 0.0393701 ft]; T_Height=301 mm; T_Height_2=258 mm; T_Height_Ref_1=43 mm  [stored 0.141076 ft]; T_Height_Ref_2=50 mm; T_ref=289 mm; Top_Profile=162 mm; Top_Profile_Ref=167 mm; W=575 mm; W_Ref=567 mm
- 879-0100-00-14400329999_DN100_PN10/16: Body_Collar_Dia=32 mm  [stored 0.104987 ft]; Body_Collar_Dia_2=22 mm  [stored 0.0721785 ft]; Body_Flange_Dia=100 mm; Body_Flange_Dia_2=109 mm; Body_Height_1=88 mm; Body_Height_2=44 mm; Body_Height_3=59 mm; Body_Height_4=59 mm; Body_Top_Dia=13 mm; Body_Top_Dia_2=11 mm  [stored 0.0360892 ft]; Body_With_Dia=44 mm; Body_With_Dia_1=88 mm; Body_With_Dia_2=88 mm; Bolt_support=269 mm; Bolt_support_2=135 mm; Bolt_support_Dia=12 mm  [stored 0.0393701 ft]; Bolt_support_lenght=70 mm; Bolt_support_lenght_2=80 mm; Bottom_profile=25 mm  [stored 0.082021 ft]; D1=78 mm; D3=110 mm; DN=100 mm; Fillet_Length=6 mm  [stored 0.019685 ft]; Fillet_Length_Ref=18 mm  [stored 0.0590551 ft]; Flange_thickness=19 mm  [stored 0.062336 ft]; H=570 mm; H3_Ref=564 mm; ID=50 mm; L=350 mm; L_Ref=156 mm; NV_Dia=100 mm; PG_Dia=50 mm; PG_Ref=58 mm; PG_depth=8 mm  [stored 0.0262467 ft]; PG_height=278 mm; PG_height_1=253 mm; PG_ref=60 mm; PR_1=66 mm; P_lenght=48 mm; Pilot_Dia_1=22 mm  [stored 0.0721785 ft]; Pilot_Dia_2=44 mm; Pilot_Dia_3=15 mm  [stored 0.0492126 ft]; Pilot_Dia_4=7 mm  [stored 0.0229659 ft]; Pilot_Dia_5=5 mm  [stored 0.0164042 ft]; Pilot_top_1=329 mm; Pilot_top_ref=115 mm; Profile1_Height=150 mm; Profile1_Length=30 mm  [stored 0.0984252 ft]; Profile1_Length_2=20 mm  [stored 0.0656168 ft]; Profile_Dia=6 mm  [stored 0.019685 ft]; Profile_Dia_2=6 mm  [stored 0.019685 ft]; Profile_Dia_3=12 mm  [stored 0.0393701 ft]; Profile_Dia_Ref=3 mm  [stored 0.00984252 ft]; Profile_Dia_Ref_2=12 mm  [stored 0.0393701 ft]; Profile_height ref=12 mm  [stored 0.0393701 ft]; T_Height=292 mm; T_Height_2=250 mm; T_Height_Ref_1=42 mm; T_Height_Ref_2=49 mm; T_ref=294 mm; Top_Profile=162 mm; Top_Profile_Ref=167 mm; W=575 mm; W_Ref=567 mm
- 879-0100-00-14400339999_DN100_PN10/16: Body_Collar_Dia=32 mm  [stored 0.104987 ft]; Body_Collar_Dia_2=22 mm  [stored 0.0721785 ft]; Body_Flange_Dia=100 mm; Body_Flange_Dia_2=109 mm; Body_Height_1=88 mm; Body_Height_2=44 mm; Body_Height_3=70 mm; Body_Height_4=59 mm; Body_Top_Dia=13 mm; Body_Top_Dia_2=11 mm  [stored 0.0360892 ft]; Body_With_Dia=44 mm; Body_With_Dia_1=88 mm; Body_With_Dia_2=88 mm; Bolt_support=269 mm; Bolt_support_2=135 mm; Bolt_support_Dia=12 mm  [stored 0.0393701 ft]; Bolt_support_lenght=70 mm; Bolt_support_lenght_2=80 mm; Bottom_profile=25 mm  [stored 0.082021 ft]; D1=78 mm; D3=110 mm; DN=101 mm; Fillet_Length=6 mm  [stored 0.019685 ft]; Fillet_Length_Ref=18 mm  [stored 0.0590551 ft]; Flange_thickness=19 mm  [stored 0.062336 ft]; H=570 mm; H3_Ref=564 mm; ID=50 mm; L=350 mm; L_Ref=156 mm; NV_Dia=100 mm; PG_Dia=50 mm; PG_Ref=58 mm; PG_depth=8 mm  [stored 0.0262467 ft]; PG_height=271 mm; PG_height_1=246 mm; PG_ref=60 mm; PR_1=68 mm; P_lenght=48 mm; Pilot_Dia_1=22 mm  [stored 0.0721785 ft]; Pilot_Dia_2=44 mm; Pilot_Dia_3=15 mm  [stored 0.0492126 ft]; Pilot_Dia_4=7 mm  [stored 0.0229659 ft]; Pilot_Dia_5=5 mm  [stored 0.0164042 ft]; Pilot_top_1=335 mm; Pilot_top_ref=109 mm; Profile1_Height=141 mm; Profile1_Length=30 mm  [stored 0.0984252 ft]; Profile1_Length_2=20 mm  [stored 0.0656168 ft]; Profile_Dia=6 mm  [stored 0.019685 ft]; Profile_Dia_2=6 mm  [stored 0.019685 ft]; Profile_Dia_3=12 mm  [stored 0.0393701 ft]; Profile_Dia_Ref=3 mm  [stored 0.00984252 ft]; Profile_Dia_Ref_2=12 mm  [stored 0.0393701 ft]; Profile_height ref=12 mm  [stored 0.0393701 ft]; T_Height=301 mm; T_Height_2=258 mm; T_Height_Ref_1=43 mm  [stored 0.141076 ft]; T_Height_Ref_2=50 mm; T_ref=289 mm; Top_Profile=162 mm; Top_Profile_Ref=167 mm; W=575 mm; W_Ref=567 mm
- 879-0125-00-14400309999_DN125_PN10/16: Body_Collar_Dia=36 mm; Body_Collar_Dia_2=25 mm  [stored 0.082021 ft]; Body_Flange_Dia=114 mm; Body_Flange_Dia_2=125 mm; Body_Height_1=100 mm; Body_Height_2=50 mm; Body_Height_3=59 mm; Body_Height_4=65 mm; Body_Top_Dia=15 mm  [stored 0.0492126 ft]; Body_Top_Dia_2=12 mm  [stored 0.0393701 ft]; Body_With_Dia=50 mm; Body_With_Dia_1=100 mm; Body_With_Dia_2=100 mm; Bolt_support=308 mm; Bolt_support_2=154 mm; Bolt_support_Dia=12 mm  [stored 0.0393701 ft]; Bolt_support_lenght=83 mm; Bolt_support_lenght_2=93 mm; Bottom_profile=31 mm  [stored 0.101706 ft]; D1=92 mm; D3=125 mm; DN=125 mm; Fillet_Length=6 mm  [stored 0.019685 ft]; Fillet_Length_Ref=18 mm  [stored 0.0590551 ft]; Flange_thickness=19 mm  [stored 0.062336 ft]; H=590 mm; H3_Ref=584 mm; ID=63 mm; L=400 mm; L_Ref=181 mm; NV_Dia=100 mm; PG_Dia=63 mm; PG_Ref=67 mm; PG_depth=8 mm  [stored 0.0262467 ft]; PG_height=307 mm; PG_height_1=276 mm; PG_ref=73 mm; PR_1=63 mm; P_lenght=61 mm; Pilot_Dia_1=28 mm; Pilot_Dia_2=55 mm; Pilot_Dia_3=18 mm  [stored 0.0590551 ft]; Pilot_Dia_4=9 mm  [stored 0.0295276 ft]; Pilot_Dia_5=6 mm  [stored 0.019685 ft]; Pilot_top_1=341 mm; Pilot_top_ref=108 mm; Profile1_Height=170 mm; Profile1_Length=34 mm; Profile1_Length_2=23 mm; Profile_Dia=6 mm  [stored 0.019685 ft]; Profile_Dia_2=6 mm  [stored 0.019685 ft]; Profile_Dia_3=12 mm  [stored 0.0393701 ft]; Profile_Dia_Ref=3 mm  [stored 0.00984252 ft]; Profile_Dia_Ref_2=12 mm  [stored 0.0393701 ft]; Profile_height ref=12 mm  [stored 0.0393701 ft]; T_Height=277 mm; T_Height_2=237 mm; T_Height_Ref_1=40 mm  [stored 0.131234 ft]; T_Height_Ref_2=46 mm; T_ref=307 mm; Top_Profile=185 mm; Top_Profile_Ref=190 mm; W=590 mm; W_Ref=582 mm
- 879-0125-00-14400319999_DN125_PN10/16: Body_Collar_Dia=36 mm; Body_Collar_Dia_2=25 mm  [stored 0.082021 ft]; Body_Flange_Dia=114 mm; Body_Flange_Dia_2=125 mm; Body_Height_1=100 mm; Body_Height_2=50 mm; Body_Height_3=70 mm; Body_Height_4=65 mm; Body_Top_Dia=15 mm  [stored 0.0492126 ft]; Body_Top_Dia_2=12 mm  [stored 0.0393701 ft]; Body_With_Dia=50 mm; Body_With_Dia_1=100 mm; Body_With_Dia_2=100 mm; Bolt_support=308 mm; Bolt_support_2=154 mm; Bolt_support_Dia=12 mm  [stored 0.0393701 ft]; Bolt_support_lenght=83 mm; Bolt_support_lenght_2=93 mm; Bottom_profile=31 mm  [stored 0.101706 ft]; D1=92 mm; D3=125 mm; DN=125 mm; Fillet_Length=6 mm  [stored 0.019685 ft]; Fillet_Length_Ref=18 mm  [stored 0.0590551 ft]; Flange_thickness=19 mm  [stored 0.062336 ft]; H=590 mm; H3_Ref=584 mm; ID=63 mm; L=400 mm; L_Ref=181 mm; NV_Dia=100 mm; PG_Dia=63 mm; PG_Ref=67 mm; PG_depth=8 mm  [stored 0.0262467 ft]; PG_height=299 mm; PG_height_1=268 mm; PG_ref=73 mm; PR_1=65 mm; P_lenght=61 mm; Pilot_Dia_1=28 mm; Pilot_Dia_2=55 mm; Pilot_Dia_3=18 mm  [stored 0.0590551 ft]; Pilot_Dia_4=9 mm  [stored 0.0295276 ft]; Pilot_Dia_5=6 mm  [stored 0.019685 ft]; Pilot_top_1=347 mm; Pilot_top_ref=102 mm; Profile1_Height=160 mm; Profile1_Length=34 mm; Profile1_Length_2=23 mm; Profile_Dia=6 mm  [stored 0.019685 ft]; Profile_Dia_2=6 mm  [stored 0.019685 ft]; Profile_Dia_3=12 mm  [stored 0.0393701 ft]; Profile_Dia_Ref=3 mm  [stored 0.00984252 ft]; Profile_Dia_Ref_2=12 mm  [stored 0.0393701 ft]; Profile_height ref=12 mm  [stored 0.0393701 ft]; T_Height=287 mm; T_Height_2=246 mm; T_Height_Ref_1=41 mm  [stored 0.134514 ft]; T_Height_Ref_2=48 mm; T_ref=302 mm; Top_Profile=185 mm; Top_Profile_Ref=190 mm; W=590 mm; W_Ref=582 mm
- 879-0125-00-144003199A0_DN125_PN10/16: Body_Collar_Dia=36 mm; Body_Collar_Dia_2=25 mm  [stored 0.082021 ft]; Body_Flange_Dia=114 mm; Body_Flange_Dia_2=125 mm; Body_Height_1=100 mm; Body_Height_2=50 mm; Body_Height_3=59 mm; Body_Height_4=65 mm; Body_Top_Dia=15 mm  [stored 0.0492126 ft]; Body_Top_Dia_2=12 mm  [stored 0.0393701 ft]; Body_With_Dia=50 mm; Body_With_Dia_1=100 mm; Body_With_Dia_2=100 mm; Bolt_support=308 mm; Bolt_support_2=154 mm; Bolt_support_Dia=12 mm  [stored 0.0393701 ft]; Bolt_support_lenght=83 mm; Bolt_support_lenght_2=93 mm; Bottom_profile=31 mm  [stored 0.101706 ft]; D1=92 mm; D3=125 mm; DN=125 mm; Fillet_Length=6 mm  [stored 0.019685 ft]; Fillet_Length_Ref=18 mm  [stored 0.0590551 ft]; Flange_thickness=19 mm  [stored 0.062336 ft]; H=590 mm; H3_Ref=584 mm; ID=63 mm; L=400 mm; L_Ref=181 mm; NV_Dia=100 mm; PG_Dia=63 mm; PG_Ref=67 mm; PG_depth=8 mm  [stored 0.0262467 ft]; PG_height=307 mm; PG_height_1=276 mm; PG_ref=73 mm; PR_1=63 mm; P_lenght=61 mm; Pilot_Dia_1=28 mm; Pilot_Dia_2=55 mm; Pilot_Dia_3=18 mm  [stored 0.0590551 ft]; Pilot_Dia_4=9 mm  [stored 0.0295276 ft]; Pilot_Dia_5=6 mm  [stored 0.019685 ft]; Pilot_top_1=341 mm; Pilot_top_ref=108 mm; Profile1_Height=170 mm; Profile1_Length=34 mm; Profile1_Length_2=23 mm; Profile_Dia=6 mm  [stored 0.019685 ft]; Profile_Dia_2=6 mm  [stored 0.019685 ft]; Profile_Dia_3=12 mm  [stored 0.0393701 ft]; Profile_Dia_Ref=3 mm  [stored 0.00984252 ft]; Profile_Dia_Ref_2=12 mm  [stored 0.0393701 ft]; Profile_height ref=12 mm  [stored 0.0393701 ft]; T_Height=277 mm; T_Height_2=237 mm; T_Height_Ref_1=40 mm  [stored 0.131234 ft]; T_Height_Ref_2=46 mm; T_ref=307 mm; Top_Profile=185 mm; Top_Profile_Ref=190 mm; W=590 mm; W_Ref=582 mm
- 879-0125-00-14400329999_DN125_PN10/16: Body_Collar_Dia=36 mm; Body_Collar_Dia_2=25 mm  [stored 0.082021 ft]; Body_Flange_Dia=114 mm; Body_Flange_Dia_2=125 mm; Body_Height_1=100 mm; Body_Height_2=50 mm; Body_Height_3=70 mm; Body_Height_4=65 mm; Body_Top_Dia=15 mm  [stored 0.0492126 ft]; Body_Top_Dia_2=12 mm  [stored 0.0393701 ft]; Body_With_Dia=50 mm; Body_With_Dia_1=100 mm; Body_With_Dia_2=100 mm; Bolt_support=308 mm; Bolt_support_2=154 mm; Bolt_support_Dia=12 mm  [stored 0.0393701 ft]; Bolt_support_lenght=83 mm; Bolt_support_lenght_2=93 mm; Bottom_profile=31 mm  [stored 0.101706 ft]; D1=92 mm; D3=125 mm; DN=125 mm; Fillet_Length=6 mm  [stored 0.019685 ft]; Fillet_Length_Ref=18 mm  [stored 0.0590551 ft]; Flange_thickness=19 mm  [stored 0.062336 ft]; H=590 mm; H3_Ref=584 mm; ID=63 mm; L=400 mm; L_Ref=181 mm; NV_Dia=100 mm; PG_Dia=63 mm; PG_Ref=67 mm; PG_depth=8 mm  [stored 0.0262467 ft]; PG_height=300 mm; PG_height_1=268 mm; PG_ref=73 mm; PR_1=65 mm; P_lenght=61 mm; Pilot_Dia_1=28 mm; Pilot_Dia_2=55 mm; Pilot_Dia_3=18 mm  [stored 0.0590551 ft]; Pilot_Dia_4=9 mm  [stored 0.0295276 ft]; Pilot_Dia_5=6 mm  [stored 0.019685 ft]; Pilot_top_1=347 mm; Pilot_top_ref=102 mm; Profile1_Height=160 mm; Profile1_Length=34 mm; Profile1_Length_2=23 mm; Profile_Dia=6 mm  [stored 0.019685 ft]; Profile_Dia_2=6 mm  [stored 0.019685 ft]; Profile_Dia_3=12 mm  [stored 0.0393701 ft]; Profile_Dia_Ref=3 mm  [stored 0.00984252 ft]; Profile_Dia_Ref_2=12 mm  [stored 0.0393701 ft]; Profile_height ref=12 mm  [stored 0.0393701 ft]; T_Height=287 mm; T_Height_2=246 mm; T_Height_Ref_1=41 mm  [stored 0.134514 ft]; T_Height_Ref_2=48 mm; T_ref=302 mm; Top_Profile=185 mm; Top_Profile_Ref=190 mm; W=590 mm; W_Ref=582 mm
- 879-0125-00-14400339999_DN125_PN10/16: Body_Collar_Dia=36 mm; Body_Collar_Dia_2=25 mm  [stored 0.082021 ft]; Body_Flange_Dia=114 mm; Body_Flange_Dia_2=125 mm; Body_Height_1=100 mm; Body_Height_2=50 mm; Body_Height_3=59 mm; Body_Height_4=65 mm; Body_Top_Dia=15 mm  [stored 0.0492126 ft]; Body_Top_Dia_2=12 mm  [stored 0.0393701 ft]; Body_With_Dia=50 mm; Body_With_Dia_1=100 mm; Body_With_Dia_2=100 mm; Bolt_support=308 mm; Bolt_support_2=154 mm; Bolt_support_Dia=12 mm  [stored 0.0393701 ft]; Bolt_support_lenght=83 mm; Bolt_support_lenght_2=93 mm; Bottom_profile=31 mm  [stored 0.101706 ft]; D1=92 mm; D3=125 mm; DN=125 mm; Fillet_Length=6 mm  [stored 0.019685 ft]; Fillet_Length_Ref=18 mm  [stored 0.0590551 ft]; Flange_thickness=19 mm  [stored 0.062336 ft]; H=590 mm; H3_Ref=584 mm; ID=63 mm; L=400 mm; L_Ref=181 mm; NV_Dia=100 mm; PG_Dia=63 mm; PG_Ref=67 mm; PG_depth=8 mm  [stored 0.0262467 ft]; PG_height=307 mm; PG_height_1=276 mm; PG_ref=73 mm; PR_1=63 mm; P_lenght=61 mm; Pilot_Dia_1=28 mm; Pilot_Dia_2=55 mm; Pilot_Dia_3=18 mm  [stored 0.0590551 ft]; Pilot_Dia_4=9 mm  [stored 0.0295276 ft]; Pilot_Dia_5=6 mm  [stored 0.019685 ft]; Pilot_top_1=341 mm; Pilot_top_ref=108 mm; Profile1_Height=170 mm; Profile1_Length=34 mm; Profile1_Length_2=23 mm; Profile_Dia=6 mm  [stored 0.019685 ft]; Profile_Dia_2=6 mm  [stored 0.019685 ft]; Profile_Dia_3=12 mm  [stored 0.0393701 ft]; Profile_Dia_Ref=3 mm  [stored 0.00984252 ft]; Profile_Dia_Ref_2=12 mm  [stored 0.0393701 ft]; Profile_height ref=12 mm  [stored 0.0393701 ft]; T_Height=277 mm; T_Height_2=237 mm; T_Height_Ref_1=40 mm  [stored 0.131234 ft]; T_Height_Ref_2=46 mm; T_ref=307 mm; Top_Profile=185 mm; Top_Profile_Ref=190 mm; W=590 mm; W_Ref=582 mm
- 879-0150-00-14400309999_DN150_PN10/16: Body_Collar_Dia=44 mm; Body_Collar_Dia_2=30 mm  [stored 0.0984252 ft]; Body_Flange_Dia=137 mm; Body_Flange_Dia_2=150 mm; Body_Height_1=120 mm; Body_Height_2=60 mm; Body_Height_3=60 mm; Body_Height_4=75 mm; Body_Top_Dia=18 mm  [stored 0.0590551 ft]; Body_Top_Dia_2=15 mm  [stored 0.0492126 ft]; Body_With_Dia=60 mm; Body_With_Dia_1=120 mm; Body_With_Dia_2=120 mm; Bolt_support=369 mm; Bolt_support_2=185 mm; Bolt_support_Dia=16 mm  [stored 0.0524934 ft]; Bolt_support_lenght=95 mm; Bolt_support_lenght_2=105 mm; Bottom_profile=38 mm; D1=106 mm; D3=143 mm; DN=150 mm; Fillet_Length=8 mm  [stored 0.0262467 ft]; Fillet_Length_Ref=24 mm  [stored 0.0787402 ft]; Flange_thickness=19 mm  [stored 0.062336 ft]; H=630 mm; H3_Ref=622 mm; ID=75 mm; L=480 mm; L_Ref=221 mm; NV_Dia=125 mm; PG_Dia=50 mm; PG_Ref=80 mm; PG_depth=11 mm  [stored 0.0360892 ft]; PG_height=325 mm; PG_height_1=300 mm; PG_ref=85 mm; PR_1=60 mm; P_lenght=68 mm; Pilot_Dia_1=31 mm  [stored 0.101706 ft]; Pilot_Dia_2=62 mm; Pilot_Dia_3=21 mm; Pilot_Dia_4=10 mm  [stored 0.0328084 ft]; Pilot_Dia_5=7 mm  [stored 0.0229659 ft]; Pilot_top_1=367 mm; Pilot_top_ref=102 mm; Profile1_Height=195 mm; Profile1_Length=39 mm  [stored 0.127953 ft]; Profile1_Length_2=26 mm; Profile_Dia=8 mm  [stored 0.0262467 ft]; Profile_Dia_2=8 mm  [stored 0.0262467 ft]; Profile_Dia_3=16 mm  [stored 0.0524934 ft]; Profile_Dia_Ref=4 mm  [stored 0.0131234 ft]; Profile_Dia_Ref_2=16 mm  [stored 0.0524934 ft]; Profile_height ref=20 mm  [stored 0.0656168 ft]; T_Height=265 mm; T_Height_2=227 mm; T_Height_Ref_1=38 mm; T_Height_Ref_2=44 mm; T_ref=335 mm; Top_Profile=222 mm; Top_Profile_Ref=227 mm; W=620 mm; W_Ref=609 mm
- 879-0150-00-14400319999_DN150_PN10/16: Body_Collar_Dia=44 mm; Body_Collar_Dia_2=30 mm  [stored 0.0984252 ft]; Body_Flange_Dia=137 mm; Body_Flange_Dia_2=150 mm; Body_Height_1=120 mm; Body_Height_2=60 mm; Body_Height_3=68 mm; Body_Height_4=75 mm; Body_Top_Dia=18 mm  [stored 0.0590551 ft]; Body_Top_Dia_2=15 mm  [stored 0.0492126 ft]; Body_With_Dia=60 mm; Body_With_Dia_1=120 mm; Body_With_Dia_2=120 mm; Bolt_support=369 mm; Bolt_support_2=185 mm; Bolt_support_Dia=16 mm  [stored 0.0524934 ft]; Bolt_support_lenght=95 mm; Bolt_support_lenght_2=105 mm; Bottom_profile=38 mm; D1=106 mm; D3=143 mm; DN=150 mm; Fillet_Length=8 mm  [stored 0.0262467 ft]; Fillet_Length_Ref=24 mm  [stored 0.0787402 ft]; Flange_thickness=19 mm  [stored 0.062336 ft]; H=630 mm; H3_Ref=622 mm; ID=75 mm; L=480 mm; L_Ref=221 mm; NV_Dia=125 mm; PG_Dia=50 mm; PG_Ref=80 mm; PG_depth=11 mm  [stored 0.0360892 ft]; PG_height=325 mm; PG_height_1=300 mm; PG_ref=85 mm; PR_1=60 mm; P_lenght=68 mm; Pilot_Dia_1=31 mm  [stored 0.101706 ft]; Pilot_Dia_2=62 mm; Pilot_Dia_3=21 mm; Pilot_Dia_4=10 mm  [stored 0.0328084 ft]; Pilot_Dia_5=7 mm  [stored 0.0229659 ft]; Pilot_top_1=371 mm; Pilot_top_ref=98 mm; Profile1_Height=195 mm; Profile1_Length=39 mm  [stored 0.127953 ft]; Profile1_Length_2=26 mm; Profile_Dia=8 mm  [stored 0.0262467 ft]; Profile_Dia_2=8 mm  [stored 0.0262467 ft]; Profile_Dia_3=16 mm  [stored 0.0524934 ft]; Profile_Dia_Ref=4 mm  [stored 0.0131234 ft]; Profile_Dia_Ref_2=16 mm  [stored 0.0524934 ft]; Profile_height ref=20 mm  [stored 0.0656168 ft]; T_Height=265 mm; T_Height_2=227 mm; T_Height_Ref_1=38 mm; T_Height_Ref_2=44 mm; T_ref=335 mm; Top_Profile=222 mm; Top_Profile_Ref=227 mm; W=620 mm; W_Ref=609 mm
- 879-0150-00-144003199A0_DN150_PN10/16: Body_Collar_Dia=44 mm; Body_Collar_Dia_2=30 mm  [stored 0.0984252 ft]; Body_Flange_Dia=137 mm; Body_Flange_Dia_2=150 mm; Body_Height_1=120 mm; Body_Height_2=60 mm; Body_Height_3=60 mm; Body_Height_4=75 mm; Body_Top_Dia=18 mm  [stored 0.0590551 ft]; Body_Top_Dia_2=15 mm  [stored 0.0492126 ft]; Body_With_Dia=60 mm; Body_With_Dia_1=120 mm; Body_With_Dia_2=120 mm; Bolt_support=369 mm; Bolt_support_2=185 mm; Bolt_support_Dia=16 mm  [stored 0.0524934 ft]; Bolt_support_lenght=95 mm; Bolt_support_lenght_2=105 mm; Bottom_profile=38 mm; D1=106 mm; D3=143 mm; DN=150 mm; Fillet_Length=8 mm  [stored 0.0262467 ft]; Fillet_Length_Ref=24 mm  [stored 0.0787402 ft]; Flange_thickness=19 mm  [stored 0.062336 ft]; H=630 mm; H3_Ref=622 mm; ID=75 mm; L=480 mm; L_Ref=221 mm; NV_Dia=125 mm; PG_Dia=50 mm; PG_Ref=80 mm; PG_depth=11 mm  [stored 0.0360892 ft]; PG_height=325 mm; PG_height_1=300 mm; PG_ref=85 mm; PR_1=60 mm; P_lenght=68 mm; Pilot_Dia_1=31 mm  [stored 0.101706 ft]; Pilot_Dia_2=62 mm; Pilot_Dia_3=21 mm; Pilot_Dia_4=10 mm  [stored 0.0328084 ft]; Pilot_Dia_5=7 mm  [stored 0.0229659 ft]; Pilot_top_1=367 mm; Pilot_top_ref=102 mm; Profile1_Height=195 mm; Profile1_Length=39 mm  [stored 0.127953 ft]; Profile1_Length_2=26 mm; Profile_Dia=8 mm  [stored 0.0262467 ft]; Profile_Dia_2=8 mm  [stored 0.0262467 ft]; Profile_Dia_3=16 mm  [stored 0.0524934 ft]; Profile_Dia_Ref=4 mm  [stored 0.0131234 ft]; Profile_Dia_Ref_2=16 mm  [stored 0.0524934 ft]; Profile_height ref=20 mm  [stored 0.0656168 ft]; T_Height=265 mm; T_Height_2=227 mm; T_Height_Ref_1=38 mm; T_Height_Ref_2=44 mm; T_ref=335 mm; Top_Profile=222 mm; Top_Profile_Ref=227 mm; W=620 mm; W_Ref=609 mm
- 879-0150-00-14400329999_DN150_PN10/16: Body_Collar_Dia=44 mm; Body_Collar_Dia_2=30 mm  [stored 0.0984252 ft]; Body_Flange_Dia=137 mm; Body_Flange_Dia_2=150 mm; Body_Height_1=120 mm; Body_Height_2=60 mm; Body_Height_3=68 mm; Body_Height_4=75 mm; Body_Top_Dia=18 mm  [stored 0.0590551 ft]; Body_Top_Dia_2=15 mm  [stored 0.0492126 ft]; Body_With_Dia=60 mm; Body_With_Dia_1=120 mm; Body_With_Dia_2=120 mm; Bolt_support=369 mm; Bolt_support_2=185 mm; Bolt_support_Dia=16 mm  [stored 0.0524934 ft]; Bolt_support_lenght=95 mm; Bolt_support_lenght_2=105 mm; Bottom_profile=38 mm; D1=106 mm; D3=143 mm; DN=150 mm; Fillet_Length=8 mm  [stored 0.0262467 ft]; Fillet_Length_Ref=24 mm  [stored 0.0787402 ft]; Flange_thickness=19 mm  [stored 0.062336 ft]; H=630 mm; H3_Ref=622 mm; ID=75 mm; L=480 mm; L_Ref=221 mm; NV_Dia=125 mm; PG_Dia=50 mm; PG_Ref=80 mm; PG_depth=11 mm  [stored 0.0360892 ft]; PG_height=325 mm; PG_height_1=300 mm; PG_ref=85 mm; PR_1=60 mm; P_lenght=68 mm; Pilot_Dia_1=31 mm  [stored 0.101706 ft]; Pilot_Dia_2=62 mm; Pilot_Dia_3=21 mm; Pilot_Dia_4=10 mm  [stored 0.0328084 ft]; Pilot_Dia_5=7 mm  [stored 0.0229659 ft]; Pilot_top_1=371 mm; Pilot_top_ref=98 mm; Profile1_Height=195 mm; Profile1_Length=39 mm  [stored 0.127953 ft]; Profile1_Length_2=26 mm; Profile_Dia=8 mm  [stored 0.0262467 ft]; Profile_Dia_2=8 mm  [stored 0.0262467 ft]; Profile_Dia_3=16 mm  [stored 0.0524934 ft]; Profile_Dia_Ref=4 mm  [stored 0.0131234 ft]; Profile_Dia_Ref_2=16 mm  [stored 0.0524934 ft]; Profile_height ref=20 mm  [stored 0.0656168 ft]; T_Height=265 mm; T_Height_2=227 mm; T_Height_Ref_1=38 mm; T_Height_Ref_2=44 mm; T_ref=335 mm; Top_Profile=222 mm; Top_Profile_Ref=227 mm; W=620 mm; W_Ref=609 mm
- 879-0150-00-14400339999_DN150_PN10/16: Body_Collar_Dia=44 mm; Body_Collar_Dia_2=30 mm  [stored 0.0984252 ft]; Body_Flange_Dia=137 mm; Body_Flange_Dia_2=150 mm; Body_Height_1=120 mm; Body_Height_2=60 mm; Body_Height_3=60 mm; Body_Height_4=75 mm; Body_Top_Dia=18 mm  [stored 0.0590551 ft]; Body_Top_Dia_2=15 mm  [stored 0.0492126 ft]; Body_With_Dia=60 mm; Body_With_Dia_1=120 mm; Body_With_Dia_2=120 mm; Bolt_support=369 mm; Bolt_support_2=185 mm; Bolt_support_Dia=16 mm  [stored 0.0524934 ft]; Bolt_support_lenght=95 mm; Bolt_support_lenght_2=105 mm; Bottom_profile=38 mm; D1=106 mm; D3=143 mm; DN=150 mm; Fillet_Length=8 mm  [stored 0.0262467 ft]; Fillet_Length_Ref=24 mm  [stored 0.0787402 ft]; Flange_thickness=19 mm  [stored 0.062336 ft]; H=630 mm; H3_Ref=622 mm; ID=75 mm; L=480 mm; L_Ref=221 mm; NV_Dia=125 mm; PG_Dia=50 mm; PG_Ref=80 mm; PG_depth=11 mm  [stored 0.0360892 ft]; PG_height=325 mm; PG_height_1=300 mm; PG_ref=85 mm; PR_1=60 mm; P_lenght=68 mm; Pilot_Dia_1=31 mm  [stored 0.101706 ft]; Pilot_Dia_2=62 mm; Pilot_Dia_3=21 mm; Pilot_Dia_4=10 mm  [stored 0.0328084 ft]; Pilot_Dia_5=7 mm  [stored 0.0229659 ft]; Pilot_top_1=367 mm; Pilot_top_ref=102 mm; Profile1_Height=195 mm; Profile1_Length=39 mm  [stored 0.127953 ft]; Profile1_Length_2=26 mm; Profile_Dia=8 mm  [stored 0.0262467 ft]; Profile_Dia_2=8 mm  [stored 0.0262467 ft]; Profile_Dia_3=16 mm  [stored 0.0524934 ft]; Profile_Dia_Ref=4 mm  [stored 0.0131234 ft]; Profile_Dia_Ref_2=16 mm  [stored 0.0524934 ft]; Profile_height ref=20 mm  [stored 0.0656168 ft]; T_Height=265 mm; T_Height_2=227 mm; T_Height_Ref_1=38 mm; T_Height_Ref_2=44 mm; T_ref=335 mm; Top_Profile=222 mm; Top_Profile_Ref=227 mm; W=620 mm; W_Ref=609 mm
- 879-0200-00-04400309999_DN200_PN10: Body_Collar_Dia=55 mm; Body_Collar_Dia_2=38 mm; Body_Flange_Dia=171 mm; Body_Flange_Dia_2=188 mm; Body_Height_1=150 mm; Body_Height_2=75 mm; Body_Height_3=75 mm; Body_Height_4=90 mm; Body_Top_Dia=22 mm  [stored 0.0721785 ft]; Body_Top_Dia_2=19 mm  [stored 0.062336 ft]; Body_With_Dia=75 mm; Body_With_Dia_1=150 mm; Body_With_Dia_2=150 mm; Bolt_support=462 mm; Bolt_support_2=231 mm; Bolt_support_Dia=20 mm  [stored 0.0656168 ft]; Bolt_support_lenght=120 mm; Bolt_support_lenght_2=130 mm; Bottom_profile=50 mm; D1=133 mm; D3=170 mm; DN=200 mm; Fillet_Length=10 mm  [stored 0.0328084 ft]; Fillet_Length_Ref=30 mm  [stored 0.0984252 ft]; Flange_thickness=20 mm  [stored 0.0656168 ft]; H=705 mm; H3_Ref=695 mm; ID=100 mm; L=600 mm; L_Ref=280 mm; NV_Dia=125 mm; PG_Dia=67 mm; PG_Ref=100 mm; PG_depth=14 mm  [stored 0.0459318 ft]; PG_height=393 mm; PG_height_1=359 mm; PG_ref=110 mm; PR_1=58 mm; P_lenght=85 mm; Pilot_Dia_1=39 mm  [stored 0.127953 ft]; Pilot_Dia_2=77 mm; Pilot_Dia_3=26 mm; Pilot_Dia_4=13 mm; Pilot_Dia_5=9 mm  [stored 0.0295276 ft]; Pilot_top_1=420 mm; Pilot_top_ref=95 mm; Profile1_Height=238 mm; Profile1_Length=46 mm; Profile1_Length_2=31 mm  [stored 0.101706 ft]; Profile_Dia=10 mm  [stored 0.0328084 ft]; Profile_Dia_2=10 mm  [stored 0.0328084 ft]; Profile_Dia_3=20 mm  [stored 0.0656168 ft]; Profile_Dia_Ref=5 mm  [stored 0.0164042 ft]; Profile_Dia_Ref_2=20 mm  [stored 0.0656168 ft]; Profile_height ref=30 mm  [stored 0.0984252 ft]; T_Height=257 mm; T_Height_2=220 mm; T_Height_Ref_1=37 mm; T_Height_Ref_2=43 mm  [stored 0.141076 ft]; T_ref=384 mm; Top_Profile=277 mm; Top_Profile_Ref=282 mm; W=710 mm; W_Ref=696 mm
- 879-0200-00-04400319999_DN200_PN10: Body_Collar_Dia=55 mm; Body_Collar_Dia_2=38 mm; Body_Flange_Dia=171 mm; Body_Flange_Dia_2=188 mm; Body_Height_1=150 mm; Body_Height_2=75 mm; Body_Height_3=100 mm; Body_Height_4=90 mm; Body_Top_Dia=22 mm  [stored 0.0721785 ft]; Body_Top_Dia_2=19 mm  [stored 0.062336 ft]; Body_With_Dia=75 mm; Body_With_Dia_1=150 mm; Body_With_Dia_2=150 mm; Bolt_support=462 mm; Bolt_support_2=231 mm; Bolt_support_Dia=20 mm  [stored 0.0656168 ft]; Bolt_support_lenght=120 mm; Bolt_support_lenght_2=130 mm; Bottom_profile=50 mm; D1=133 mm; D3=170 mm; DN=200 mm; Fillet_Length=10 mm  [stored 0.0328084 ft]; Fillet_Length_Ref=30 mm  [stored 0.0984252 ft]; Flange_thickness=20 mm  [stored 0.0656168 ft]; H=705 mm; H3_Ref=695 mm; ID=100 mm; L=600 mm; L_Ref=280 mm; NV_Dia=125 mm; PG_Dia=67 mm; PG_Ref=100 mm; PG_depth=14 mm  [stored 0.0459318 ft]; PG_height=394 mm; PG_height_1=361 mm; PG_ref=110 mm; PR_1=58 mm; P_lenght=85 mm; Pilot_Dia_1=39 mm  [stored 0.127953 ft]; Pilot_Dia_2=77 mm; Pilot_Dia_3=26 mm; Pilot_Dia_4=13 mm; Pilot_Dia_5=9 mm  [stored 0.0295276 ft]; Pilot_top_1=433 mm; Pilot_top_ref=83 mm; Profile1_Height=240 mm; Profile1_Length=46 mm; Profile1_Length_2=31 mm  [stored 0.101706 ft]; Profile_Dia=10 mm  [stored 0.0328084 ft]; Profile_Dia_2=10 mm  [stored 0.0328084 ft]; Profile_Dia_3=20 mm  [stored 0.0656168 ft]; Profile_Dia_Ref=5 mm  [stored 0.0164042 ft]; Profile_Dia_Ref_2=20 mm  [stored 0.0656168 ft]; Profile_height ref=30 mm  [stored 0.0984252 ft]; T_Height=255 mm; T_Height_2=219 mm; T_Height_Ref_1=36 mm; T_Height_Ref_2=43 mm  [stored 0.141076 ft]; T_ref=385 mm; Top_Profile=277 mm; Top_Profile_Ref=282 mm; W=710 mm; W_Ref=696 mm
- 879-0200-00-044003199A0_DN200_PN10: Body_Collar_Dia=55 mm; Body_Collar_Dia_2=38 mm; Body_Flange_Dia=171 mm; Body_Flange_Dia_2=188 mm; Body_Height_1=150 mm; Body_Height_2=75 mm; Body_Height_3=75 mm; Body_Height_4=90 mm; Body_Top_Dia=22 mm  [stored 0.0721785 ft]; Body_Top_Dia_2=19 mm  [stored 0.062336 ft]; Body_With_Dia=75 mm; Body_With_Dia_1=150 mm; Body_With_Dia_2=150 mm; Bolt_support=462 mm; Bolt_support_2=231 mm; Bolt_support_Dia=20 mm  [stored 0.0656168 ft]; Bolt_support_lenght=120 mm; Bolt_support_lenght_2=130 mm; Bottom_profile=50 mm; D1=133 mm; D3=170 mm; DN=200 mm; Fillet_Length=10 mm  [stored 0.0328084 ft]; Fillet_Length_Ref=30 mm  [stored 0.0984252 ft]; Flange_thickness=20 mm  [stored 0.0656168 ft]; H=705 mm; H3_Ref=695 mm; ID=100 mm; L=600 mm; L_Ref=280 mm; NV_Dia=125 mm; PG_Dia=67 mm; PG_Ref=100 mm; PG_depth=14 mm  [stored 0.0459318 ft]; PG_height=393 mm; PG_height_1=359 mm; PG_ref=110 mm; PR_1=58 mm; P_lenght=85 mm; Pilot_Dia_1=39 mm  [stored 0.127953 ft]; Pilot_Dia_2=77 mm; Pilot_Dia_3=26 mm; Pilot_Dia_4=13 mm; Pilot_Dia_5=9 mm  [stored 0.0295276 ft]; Pilot_top_1=420 mm; Pilot_top_ref=95 mm; Profile1_Height=238 mm; Profile1_Length=46 mm; Profile1_Length_2=31 mm  [stored 0.101706 ft]; Profile_Dia=10 mm  [stored 0.0328084 ft]; Profile_Dia_2=10 mm  [stored 0.0328084 ft]; Profile_Dia_3=20 mm  [stored 0.0656168 ft]; Profile_Dia_Ref=5 mm  [stored 0.0164042 ft]; Profile_Dia_Ref_2=20 mm  [stored 0.0656168 ft]; Profile_height ref=30 mm  [stored 0.0984252 ft]; T_Height=257 mm; T_Height_2=220 mm; T_Height_Ref_1=37 mm; T_Height_Ref_2=43 mm  [stored 0.141076 ft]; T_ref=384 mm; Top_Profile=277 mm; Top_Profile_Ref=282 mm; W=710 mm; W_Ref=696 mm
- 879-0200-00-04400329999_DN200_PN10: Body_Collar_Dia=55 mm; Body_Collar_Dia_2=38 mm; Body_Flange_Dia=171 mm; Body_Flange_Dia_2=188 mm; Body_Height_1=150 mm; Body_Height_2=75 mm; Body_Height_3=86 mm; Body_Height_4=90 mm; Body_Top_Dia=22 mm  [stored 0.0721785 ft]; Body_Top_Dia_2=19 mm  [stored 0.062336 ft]; Body_With_Dia=75 mm; Body_With_Dia_1=150 mm; Body_With_Dia_2=150 mm; Bolt_support=462 mm; Bolt_support_2=231 mm; Bolt_support_Dia=20 mm  [stored 0.0656168 ft]; Bolt_support_lenght=120 mm; Bolt_support_lenght_2=130 mm; Bottom_profile=50 mm; D1=133 mm; D3=170 mm; DN=200 mm; Fillet_Length=10 mm  [stored 0.0328084 ft]; Fillet_Length_Ref=30 mm  [stored 0.0984252 ft]; Flange_thickness=20 mm  [stored 0.0656168 ft]; H=705 mm; H3_Ref=695 mm; ID=100 mm; L=600 mm; L_Ref=280 mm; NV_Dia=125 mm; PG_Dia=67 mm; PG_Ref=100 mm; PG_depth=14 mm  [stored 0.0459318 ft]; PG_height=394 mm; PG_height_1=361 mm; PG_ref=110 mm; PR_1=58 mm; P_lenght=85 mm; Pilot_Dia_1=39 mm  [stored 0.127953 ft]; Pilot_Dia_2=77 mm; Pilot_Dia_3=26 mm; Pilot_Dia_4=13 mm; Pilot_Dia_5=9 mm  [stored 0.0295276 ft]; Pilot_top_1=426 mm; Pilot_top_ref=90 mm; Profile1_Height=240 mm; Profile1_Length=46 mm; Profile1_Length_2=31 mm  [stored 0.101706 ft]; Profile_Dia=10 mm  [stored 0.0328084 ft]; Profile_Dia_2=10 mm  [stored 0.0328084 ft]; Profile_Dia_3=20 mm  [stored 0.0656168 ft]; Profile_Dia_Ref=5 mm  [stored 0.0164042 ft]; Profile_Dia_Ref_2=20 mm  [stored 0.0656168 ft]; Profile_height ref=30 mm  [stored 0.0984252 ft]; T_Height=255 mm; T_Height_2=219 mm; T_Height_Ref_1=36 mm; T_Height_Ref_2=43 mm  [stored 0.141076 ft]; T_ref=385 mm; Top_Profile=277 mm; Top_Profile_Ref=282 mm; W=710 mm; W_Ref=696 mm
- 879-0200-00-04400339999_DN200_PN10: Body_Collar_Dia=55 mm; Body_Collar_Dia_2=38 mm; Body_Flange_Dia=171 mm; Body_Flange_Dia_2=188 mm; Body_Height_1=150 mm; Body_Height_2=75 mm; Body_Height_3=75 mm; Body_Height_4=90 mm; Body_Top_Dia=22 mm  [stored 0.0721785 ft]; Body_Top_Dia_2=19 mm  [stored 0.062336 ft]; Body_With_Dia=75 mm; Body_With_Dia_1=150 mm; Body_With_Dia_2=150 mm; Bolt_support=462 mm; Bolt_support_2=231 mm; Bolt_support_Dia=20 mm  [stored 0.0656168 ft]; Bolt_support_lenght=120 mm; Bolt_support_lenght_2=130 mm; Bottom_profile=50 mm; D1=133 mm; D3=170 mm; DN=200 mm; Fillet_Length=10 mm  [stored 0.0328084 ft]; Fillet_Length_Ref=30 mm  [stored 0.0984252 ft]; Flange_thickness=20 mm  [stored 0.0656168 ft]; H=705 mm; H3_Ref=695 mm; ID=100 mm; L=600 mm; L_Ref=280 mm; NV_Dia=125 mm; PG_Dia=67 mm; PG_Ref=100 mm; PG_depth=14 mm  [stored 0.0459318 ft]; PG_height=393 mm; PG_height_1=360 mm; PG_ref=110 mm; PR_1=58 mm; P_lenght=85 mm; Pilot_Dia_1=39 mm  [stored 0.127953 ft]; Pilot_Dia_2=77 mm; Pilot_Dia_3=26 mm; Pilot_Dia_4=13 mm; Pilot_Dia_5=9 mm  [stored 0.0295276 ft]; Pilot_top_1=420 mm; Pilot_top_ref=95 mm; Profile1_Height=238 mm; Profile1_Length=46 mm; Profile1_Length_2=31 mm  [stored 0.101706 ft]; Profile_Dia=10 mm  [stored 0.0328084 ft]; Profile_Dia_2=10 mm  [stored 0.0328084 ft]; Profile_Dia_3=20 mm  [stored 0.0656168 ft]; Profile_Dia_Ref=5 mm  [stored 0.0164042 ft]; Profile_Dia_Ref_2=20 mm  [stored 0.0656168 ft]; Profile_height ref=30 mm  [stored 0.0984252 ft]; T_Height=257 mm; T_Height_2=220 mm; T_Height_Ref_1=37 mm; T_Height_Ref_2=43 mm  [stored 0.141076 ft]; T_ref=384 mm; Top_Profile=277 mm; Top_Profile_Ref=282 mm; W=710 mm; W_Ref=696 mm
- 879-0200-00-14400309999_DN200_PN16: Body_Collar_Dia=55 mm; Body_Collar_Dia_2=38 mm; Body_Flange_Dia=171 mm; Body_Flange_Dia_2=188 mm; Body_Height_1=150 mm; Body_Height_2=75 mm; Body_Height_3=100 mm; Body_Height_4=90 mm; Body_Top_Dia=22 mm  [stored 0.0721785 ft]; Body_Top_Dia_2=19 mm  [stored 0.062336 ft]; Body_With_Dia=75 mm; Body_With_Dia_1=150 mm; Body_With_Dia_2=150 mm; Bolt_support=462 mm; Bolt_support_2=231 mm; Bolt_support_Dia=20 mm  [stored 0.0656168 ft]; Bolt_support_lenght=120 mm; Bolt_support_lenght_2=130 mm; Bottom_profile=50 mm; D1=133 mm; D3=170 mm; DN=201 mm; Fillet_Length=10 mm  [stored 0.0328084 ft]; Fillet_Length_Ref=30 mm  [stored 0.0984252 ft]; Flange_thickness=20 mm  [stored 0.0656168 ft]; H=705 mm; H3_Ref=695 mm; ID=100 mm; L=600 mm; L_Ref=280 mm; NV_Dia=125 mm; PG_Dia=67 mm; PG_Ref=100 mm; PG_depth=14 mm  [stored 0.0459318 ft]; PG_height=395 mm; PG_height_1=361 mm; PG_ref=110 mm; PR_1=58 mm; P_lenght=85 mm; Pilot_Dia_1=39 mm  [stored 0.127953 ft]; Pilot_Dia_2=77 mm; Pilot_Dia_3=26 mm; Pilot_Dia_4=13 mm; Pilot_Dia_5=9 mm  [stored 0.0295276 ft]; Pilot_top_1=433 mm; Pilot_top_ref=83 mm; Profile1_Height=240 mm; Profile1_Length=46 mm; Profile1_Length_2=31 mm  [stored 0.101706 ft]; Profile_Dia=10 mm  [stored 0.0328084 ft]; Profile_Dia_2=10 mm  [stored 0.0328084 ft]; Profile_Dia_3=20 mm  [stored 0.0656168 ft]; Profile_Dia_Ref=5 mm  [stored 0.0164042 ft]; Profile_Dia_Ref_2=20 mm  [stored 0.0656168 ft]; Profile_height ref=30 mm  [stored 0.0984252 ft]; T_Height=255 mm; T_Height_2=219 mm; T_Height_Ref_1=36 mm; T_Height_Ref_2=43 mm  [stored 0.141076 ft]; T_ref=385 mm; Top_Profile=277 mm; Top_Profile_Ref=282 mm; W=710 mm; W_Ref=696 mm
- 879-0200-00-14400319999_DN200_PN16: Body_Collar_Dia=55 mm; Body_Collar_Dia_2=38 mm; Body_Flange_Dia=171 mm; Body_Flange_Dia_2=188 mm; Body_Height_1=150 mm; Body_Height_2=75 mm; Body_Height_3=75 mm; Body_Height_4=90 mm; Body_Top_Dia=22 mm  [stored 0.0721785 ft]; Body_Top_Dia_2=19 mm  [stored 0.062336 ft]; Body_With_Dia=75 mm; Body_With_Dia_1=150 mm; Body_With_Dia_2=150 mm; Bolt_support=462 mm; Bolt_support_2=231 mm; Bolt_support_Dia=20 mm  [stored 0.0656168 ft]; Bolt_support_lenght=120 mm; Bolt_support_lenght_2=130 mm; Bottom_profile=50 mm; D1=133 mm; D3=170 mm; DN=201 mm; Fillet_Length=10 mm  [stored 0.0328084 ft]; Fillet_Length_Ref=30 mm  [stored 0.0984252 ft]; Flange_thickness=20 mm  [stored 0.0656168 ft]; H=705 mm; H3_Ref=695 mm; ID=100 mm; L=600 mm; L_Ref=280 mm; NV_Dia=125 mm; PG_Dia=67 mm; PG_Ref=100 mm; PG_depth=14 mm  [stored 0.0459318 ft]; PG_height=393 mm; PG_height_1=360 mm; PG_ref=110 mm; PR_1=58 mm; P_lenght=85 mm; Pilot_Dia_1=39 mm  [stored 0.127953 ft]; Pilot_Dia_2=77 mm; Pilot_Dia_3=26 mm; Pilot_Dia_4=13 mm; Pilot_Dia_5=9 mm  [stored 0.0295276 ft]; Pilot_top_1=420 mm; Pilot_top_ref=95 mm; Profile1_Height=238 mm; Profile1_Length=46 mm; Profile1_Length_2=31 mm  [stored 0.101706 ft]; Profile_Dia=10 mm  [stored 0.0328084 ft]; Profile_Dia_2=10 mm  [stored 0.0328084 ft]; Profile_Dia_3=20 mm  [stored 0.0656168 ft]; Profile_Dia_Ref=5 mm  [stored 0.0164042 ft]; Profile_Dia_Ref_2=20 mm  [stored 0.0656168 ft]; Profile_height ref=30 mm  [stored 0.0984252 ft]; T_Height=257 mm; T_Height_2=220 mm; T_Height_Ref_1=37 mm; T_Height_Ref_2=43 mm  [stored 0.141076 ft]; T_ref=384 mm; Top_Profile=277 mm; Top_Profile_Ref=282 mm; W=710 mm; W_Ref=696 mm
- 879-0200-00-144003199A0_DN200_PN16: Body_Collar_Dia=55 mm; Body_Collar_Dia_2=38 mm; Body_Flange_Dia=171 mm; Body_Flange_Dia_2=188 mm; Body_Height_1=150 mm; Body_Height_2=75 mm; Body_Height_3=86 mm; Body_Height_4=90 mm; Body_Top_Dia=22 mm  [stored 0.0721785 ft]; Body_Top_Dia_2=19 mm  [stored 0.062336 ft]; Body_With_Dia=75 mm; Body_With_Dia_1=150 mm; Body_With_Dia_2=150 mm; Bolt_support=462 mm; Bolt_support_2=231 mm; Bolt_support_Dia=20 mm  [stored 0.0656168 ft]; Bolt_support_lenght=120 mm; Bolt_support_lenght_2=130 mm; Bottom_profile=50 mm; D1=133 mm; D3=170 mm; DN=201 mm; Fillet_Length=10 mm  [stored 0.0328084 ft]; Fillet_Length_Ref=30 mm  [stored 0.0984252 ft]; Flange_thickness=20 mm  [stored 0.0656168 ft]; H=705 mm; H3_Ref=695 mm; ID=100 mm; L=600 mm; L_Ref=280 mm; NV_Dia=125 mm; PG_Dia=67 mm; PG_Ref=100 mm; PG_depth=14 mm  [stored 0.0459318 ft]; PG_height=395 mm; PG_height_1=361 mm; PG_ref=110 mm; PR_1=58 mm; P_lenght=85 mm; Pilot_Dia_1=39 mm  [stored 0.127953 ft]; Pilot_Dia_2=77 mm; Pilot_Dia_3=26 mm; Pilot_Dia_4=13 mm; Pilot_Dia_5=9 mm  [stored 0.0295276 ft]; Pilot_top_1=426 mm; Pilot_top_ref=90 mm; Profile1_Height=240 mm; Profile1_Length=46 mm; Profile1_Length_2=31 mm  [stored 0.101706 ft]; Profile_Dia=10 mm  [stored 0.0328084 ft]; Profile_Dia_2=10 mm  [stored 0.0328084 ft]; Profile_Dia_3=20 mm  [stored 0.0656168 ft]; Profile_Dia_Ref=5 mm  [stored 0.0164042 ft]; Profile_Dia_Ref_2=20 mm  [stored 0.0656168 ft]; Profile_height ref=30 mm  [stored 0.0984252 ft]; T_Height=255 mm; T_Height_2=219 mm; T_Height_Ref_1=36 mm; T_Height_Ref_2=43 mm  [stored 0.141076 ft]; T_ref=385 mm; Top_Profile=277 mm; Top_Profile_Ref=282 mm; W=710 mm; W_Ref=696 mm
- 879-0200-00-14400329999_DN200_PN16: Body_Collar_Dia=55 mm; Body_Collar_Dia_2=38 mm; Body_Flange_Dia=171 mm; Body_Flange_Dia_2=188 mm; Body_Height_1=150 mm; Body_Height_2=75 mm; Body_Height_3=75 mm; Body_Height_4=90 mm; Body_Top_Dia=22 mm  [stored 0.0721785 ft]; Body_Top_Dia_2=19 mm  [stored 0.062336 ft]; Body_With_Dia=75 mm; Body_With_Dia_1=150 mm; Body_With_Dia_2=150 mm; Bolt_support=462 mm; Bolt_support_2=231 mm; Bolt_support_Dia=20 mm  [stored 0.0656168 ft]; Bolt_support_lenght=120 mm; Bolt_support_lenght_2=130 mm; Bottom_profile=50 mm; D1=133 mm; D3=170 mm; DN=201 mm; Fillet_Length=10 mm  [stored 0.0328084 ft]; Fillet_Length_Ref=30 mm  [stored 0.0984252 ft]; Flange_thickness=20 mm  [stored 0.0656168 ft]; H=705 mm; H3_Ref=695 mm; ID=100 mm; L=600 mm; L_Ref=280 mm; NV_Dia=125 mm; PG_Dia=67 mm; PG_Ref=100 mm; PG_depth=14 mm  [stored 0.0459318 ft]; PG_height=393 mm; PG_height_1=360 mm; PG_ref=110 mm; PR_1=58 mm; P_lenght=85 mm; Pilot_Dia_1=39 mm  [stored 0.127953 ft]; Pilot_Dia_2=77 mm; Pilot_Dia_3=26 mm; Pilot_Dia_4=13 mm; Pilot_Dia_5=9 mm  [stored 0.0295276 ft]; Pilot_top_1=420 mm; Pilot_top_ref=95 mm; Profile1_Height=238 mm; Profile1_Length=46 mm; Profile1_Length_2=31 mm  [stored 0.101706 ft]; Profile_Dia=10 mm  [stored 0.0328084 ft]; Profile_Dia_2=10 mm  [stored 0.0328084 ft]; Profile_Dia_3=20 mm  [stored 0.0656168 ft]; Profile_Dia_Ref=5 mm  [stored 0.0164042 ft]; Profile_Dia_Ref_2=20 mm  [stored 0.0656168 ft]; Profile_height ref=30 mm  [stored 0.0984252 ft]; T_Height=257 mm; T_Height_2=220 mm; T_Height_Ref_1=37 mm; T_Height_Ref_2=43 mm  [stored 0.141076 ft]; T_ref=384 mm; Top_Profile=277 mm; Top_Profile_Ref=282 mm; W=710 mm; W_Ref=696 mm
- 879-0200-00-14400339999_DN200_PN16: Body_Collar_Dia=55 mm; Body_Collar_Dia_2=38 mm; Body_Flange_Dia=171 mm; Body_Flange_Dia_2=188 mm; Body_Height_1=150 mm; Body_Height_2=75 mm; Body_Height_3=100 mm; Body_Height_4=90 mm; Body_Top_Dia=22 mm  [stored 0.0721785 ft]; Body_Top_Dia_2=19 mm  [stored 0.062336 ft]; Body_With_Dia=75 mm; Body_With_Dia_1=150 mm; Body_With_Dia_2=150 mm; Bolt_support=462 mm; Bolt_support_2=231 mm; Bolt_support_Dia=20 mm  [stored 0.0656168 ft]; Bolt_support_lenght=120 mm; Bolt_support_lenght_2=130 mm; Bottom_profile=50 mm; D1=133 mm; D3=170 mm; DN=201 mm; Fillet_Length=10 mm  [stored 0.0328084 ft]; Fillet_Length_Ref=30 mm  [stored 0.0984252 ft]; Flange_thickness=20 mm  [stored 0.0656168 ft]; H=705 mm; H3_Ref=695 mm; ID=100 mm; L=600 mm; L_Ref=280 mm; NV_Dia=125 mm; PG_Dia=67 mm; PG_Ref=100 mm; PG_depth=14 mm  [stored 0.0459318 ft]; PG_height=395 mm; PG_height_1=361 mm; PG_ref=110 mm; PR_1=58 mm; P_lenght=85 mm; Pilot_Dia_1=39 mm  [stored 0.127953 ft]; Pilot_Dia_2=77 mm; Pilot_Dia_3=26 mm; Pilot_Dia_4=13 mm; Pilot_Dia_5=9 mm  [stored 0.0295276 ft]; Pilot_top_1=433 mm; Pilot_top_ref=83 mm; Profile1_Height=240 mm; Profile1_Length=46 mm; Profile1_Length_2=31 mm  [stored 0.101706 ft]; Profile_Dia=10 mm  [stored 0.0328084 ft]; Profile_Dia_2=10 mm  [stored 0.0328084 ft]; Profile_Dia_3=20 mm  [stored 0.0656168 ft]; Profile_Dia_Ref=5 mm  [stored 0.0164042 ft]; Profile_Dia_Ref_2=20 mm  [stored 0.0656168 ft]; Profile_height ref=30 mm  [stored 0.0984252 ft]; T_Height=255 mm; T_Height_2=219 mm; T_Height_Ref_1=36 mm; T_Height_Ref_2=43 mm  [stored 0.141076 ft]; T_ref=385 mm; Top_Profile=277 mm; Top_Profile_Ref=282 mm; W=710 mm; W_Ref=696 mm
- 879-0250-00-04400309999_DN250_PN10: Body_Collar_Dia=66 mm; Body_Collar_Dia_2=46 mm; Body_Flange_Dia=209 mm; Body_Flange_Dia_2=228 mm; Body_Height_1=183 mm; Body_Height_2=91 mm; Body_Height_3=81 mm; Body_Height_4=106 mm; Body_Top_Dia=27 mm  [stored 0.0885827 ft]; Body_Top_Dia_2=23 mm; Body_With_Dia=91 mm; Body_With_Dia_1=183 mm; Body_With_Dia_2=183 mm; Bolt_support=562 mm; Bolt_support_2=281 mm; Bolt_support_Dia=20 mm  [stored 0.0656168 ft]; Bolt_support_lenght=145 mm; Bolt_support_lenght_2=155 mm; Bottom_profile=63 mm; D1=160 mm; D3=198 mm; DN=250 mm; Fillet_Length=10 mm  [stored 0.0328084 ft]; Fillet_Length_Ref=30 mm  [stored 0.0984252 ft]; Flange_thickness=22 mm  [stored 0.0721785 ft]; H=800 mm; H3_Ref=790 mm; ID=125 mm; L=730 mm; L_Ref=343 mm; NV_Dia=170 mm; PG_Dia=83 mm; PG_Ref=122 mm; PG_depth=14 mm  [stored 0.0459318 ft]; PG_height=467 mm; PG_height_1=425 mm; PG_ref=135 mm; PR_1=61 mm; P_lenght=101 mm; Pilot_Dia_1=46 mm; Pilot_Dia_2=92 mm; Pilot_Dia_3=31 mm  [stored 0.101706 ft]; Pilot_Dia_4=15 mm  [stored 0.0492126 ft]; Pilot_Dia_5=10 mm  [stored 0.0328084 ft]; Pilot_top_1=481 mm; Pilot_top_ref=101 mm; Profile1_Height=292 mm; Profile1_Length=53 mm; Profile1_Length_2=36 mm; Profile_Dia=10 mm  [stored 0.0328084 ft]; Profile_Dia_2=10 mm  [stored 0.0328084 ft]; Profile_Dia_3=20 mm  [stored 0.0656168 ft]; Profile_Dia_Ref=5 mm  [stored 0.0164042 ft]; Profile_Dia_Ref_2=20 mm  [stored 0.0656168 ft]; Profile_height ref=30 mm  [stored 0.0984252 ft]; T_Height=271 mm; T_Height_2=232 mm; T_Height_Ref_1=39 mm  [stored 0.127953 ft]; T_Height_Ref_2=45 mm; T_ref=444 mm; Top_Profile=337 mm; Top_Profile_Ref=342 mm; W=765 mm; W_Ref=751 mm
- 879-0250-00-04400319999_DN250_PN10: Body_Collar_Dia=66 mm; Body_Collar_Dia_2=46 mm; Body_Flange_Dia=209 mm; Body_Flange_Dia_2=228 mm; Body_Height_1=183 mm; Body_Height_2=91 mm; Body_Height_3=105 mm; Body_Height_4=106 mm; Body_Top_Dia=27 mm  [stored 0.0885827 ft]; Body_Top_Dia_2=23 mm; Body_With_Dia=91 mm; Body_With_Dia_1=183 mm; Body_With_Dia_2=183 mm; Bolt_support=562 mm; Bolt_support_2=281 mm; Bolt_support_Dia=20 mm  [stored 0.0656168 ft]; Bolt_support_lenght=145 mm; Bolt_support_lenght_2=155 mm; Bottom_profile=63 mm; D1=160 mm; D3=198 mm; DN=250 mm; Fillet_Length=10 mm  [stored 0.0328084 ft]; Fillet_Length_Ref=30 mm  [stored 0.0984252 ft]; Flange_thickness=22 mm  [stored 0.0721785 ft]; H=800 mm; H3_Ref=790 mm; ID=125 mm; L=730 mm; L_Ref=343 mm; NV_Dia=170 mm; PG_Dia=83 mm; PG_Ref=122 mm; PG_depth=14 mm  [stored 0.0459318 ft]; PG_height=469 mm; PG_height_1=427 mm; PG_ref=135 mm; PR_1=61 mm; P_lenght=101 mm; Pilot_Dia_1=46 mm; Pilot_Dia_2=92 mm; Pilot_Dia_3=31 mm  [stored 0.101706 ft]; Pilot_Dia_4=15 mm  [stored 0.0492126 ft]; Pilot_Dia_5=10 mm  [stored 0.0328084 ft]; Pilot_top_1=493 mm; Pilot_top_ref=90 mm; Profile1_Height=295 mm; Profile1_Length=53 mm; Profile1_Length_2=36 mm; Profile_Dia=10 mm  [stored 0.0328084 ft]; Profile_Dia_2=10 mm  [stored 0.0328084 ft]; Profile_Dia_3=20 mm  [stored 0.0656168 ft]; Profile_Dia_Ref=5 mm  [stored 0.0164042 ft]; Profile_Dia_Ref_2=20 mm  [stored 0.0656168 ft]; Profile_height ref=30 mm  [stored 0.0984252 ft]; T_Height=268 mm; T_Height_2=229 mm; T_Height_Ref_1=38 mm; T_Height_Ref_2=45 mm; T_ref=446 mm; Top_Profile=337 mm; Top_Profile_Ref=342 mm; W=765 mm; W_Ref=751 mm
- 879-0250-00-044003199A0_DN250_PN10: Body_Collar_Dia=66 mm; Body_Collar_Dia_2=46 mm; Body_Flange_Dia=209 mm; Body_Flange_Dia_2=228 mm; Body_Height_1=183 mm; Body_Height_2=91 mm; Body_Height_3=81 mm; Body_Height_4=106 mm; Body_Top_Dia=27 mm  [stored 0.0885827 ft]; Body_Top_Dia_2=23 mm; Body_With_Dia=91 mm; Body_With_Dia_1=183 mm; Body_With_Dia_2=183 mm; Bolt_support=562 mm; Bolt_support_2=281 mm; Bolt_support_Dia=20 mm  [stored 0.0656168 ft]; Bolt_support_lenght=145 mm; Bolt_support_lenght_2=155 mm; Bottom_profile=63 mm; D1=160 mm; D3=198 mm; DN=250 mm; Fillet_Length=10 mm  [stored 0.0328084 ft]; Fillet_Length_Ref=30 mm  [stored 0.0984252 ft]; Flange_thickness=22 mm  [stored 0.0721785 ft]; H=806 mm; H3_Ref=796 mm; ID=125 mm; L=730 mm; L_Ref=343 mm; NV_Dia=170 mm; PG_Dia=83 mm; PG_Ref=122 mm; PG_depth=14 mm  [stored 0.0459318 ft]; PG_height=474 mm; PG_height_1=432 mm; PG_ref=135 mm; PR_1=61 mm; P_lenght=103 mm; Pilot_Dia_1=47 mm; Pilot_Dia_2=94 mm; Pilot_Dia_3=31 mm  [stored 0.101706 ft]; Pilot_Dia_4=16 mm  [stored 0.0524934 ft]; Pilot_Dia_5=10 mm  [stored 0.0328084 ft]; Pilot_top_1=484 mm; Pilot_top_ref=104 mm; Profile1_Height=300 mm; Profile1_Length=53 mm; Profile1_Length_2=36 mm; Profile_Dia=10 mm  [stored 0.0328084 ft]; Profile_Dia_2=10 mm  [stored 0.0328084 ft]; Profile_Dia_3=20 mm  [stored 0.0656168 ft]; Profile_Dia_Ref=5 mm  [stored 0.0164042 ft]; Profile_Dia_Ref_2=20 mm  [stored 0.0656168 ft]; Profile_height ref=30 mm  [stored 0.0984252 ft]; T_Height=269 mm; T_Height_2=230 mm; T_Height_Ref_1=38 mm; T_Height_Ref_2=45 mm; T_ref=451 mm; Top_Profile=337 mm; Top_Profile_Ref=342 mm; W=765 mm; W_Ref=751 mm
- 879-0250-00-04400329999_DN250_PN10: Body_Collar_Dia=66 mm; Body_Collar_Dia_2=46 mm; Body_Flange_Dia=209 mm; Body_Flange_Dia_2=228 mm; Body_Height_1=183 mm; Body_Height_2=91 mm; Body_Height_3=81 mm; Body_Height_4=106 mm; Body_Top_Dia=27 mm  [stored 0.0885827 ft]; Body_Top_Dia_2=23 mm; Body_With_Dia=91 mm; Body_With_Dia_1=183 mm; Body_With_Dia_2=183 mm; Bolt_support=562 mm; Bolt_support_2=281 mm; Bolt_support_Dia=20 mm  [stored 0.0656168 ft]; Bolt_support_lenght=145 mm; Bolt_support_lenght_2=155 mm; Bottom_profile=63 mm; D1=160 mm; D3=198 mm; DN=250 mm; Fillet_Length=10 mm  [stored 0.0328084 ft]; Fillet_Length_Ref=30 mm  [stored 0.0984252 ft]; Flange_thickness=22 mm  [stored 0.0721785 ft]; H=800 mm; H3_Ref=790 mm; ID=125 mm; L=730 mm; L_Ref=343 mm; NV_Dia=170 mm; PG_Dia=83 mm; PG_Ref=122 mm; PG_depth=14 mm  [stored 0.0459318 ft]; PG_height=484 mm; PG_height_1=443 mm; PG_ref=135 mm; PR_1=56 mm; P_lenght=103 mm; Pilot_Dia_1=47 mm; Pilot_Dia_2=94 mm; Pilot_Dia_3=31 mm  [stored 0.101706 ft]; Pilot_Dia_4=16 mm  [stored 0.0524934 ft]; Pilot_Dia_5=10 mm  [stored 0.0328084 ft]; Pilot_top_1=481 mm; Pilot_top_ref=101 mm; Profile1_Height=315 mm; Profile1_Length=53 mm; Profile1_Length_2=36 mm; Profile_Dia=10 mm  [stored 0.0328084 ft]; Profile_Dia_2=10 mm  [stored 0.0328084 ft]; Profile_Dia_3=20 mm  [stored 0.0656168 ft]; Profile_Dia_Ref=5 mm  [stored 0.0164042 ft]; Profile_Dia_Ref_2=20 mm  [stored 0.0656168 ft]; Profile_height ref=30 mm  [stored 0.0984252 ft]; T_Height=248 mm; T_Height_2=212 mm; T_Height_Ref_1=35 mm  [stored 0.114829 ft]; T_Height_Ref_2=41 mm  [stored 0.134514 ft]; T_ref=457 mm; Top_Profile=337 mm; Top_Profile_Ref=342 mm; W=765 mm; W_Ref=751 mm
- 879-0250-00-04400339999_DN250_PN10: Body_Collar_Dia=66 mm; Body_Collar_Dia_2=46 mm; Body_Flange_Dia=209 mm; Body_Flange_Dia_2=228 mm; Body_Height_1=183 mm; Body_Height_2=91 mm; Body_Height_3=81 mm; Body_Height_4=106 mm; Body_Top_Dia=27 mm  [stored 0.0885827 ft]; Body_Top_Dia_2=23 mm; Body_With_Dia=91 mm; Body_With_Dia_1=183 mm; Body_With_Dia_2=183 mm; Bolt_support=562 mm; Bolt_support_2=281 mm; Bolt_support_Dia=20 mm  [stored 0.0656168 ft]; Bolt_support_lenght=145 mm; Bolt_support_lenght_2=155 mm; Bottom_profile=63 mm; D1=160 mm; D3=198 mm; DN=250 mm; Fillet_Length=10 mm  [stored 0.0328084 ft]; Fillet_Length_Ref=30 mm  [stored 0.0984252 ft]; Flange_thickness=22 mm  [stored 0.0721785 ft]; H=800 mm; H3_Ref=790 mm; ID=125 mm; L=730 mm; L_Ref=343 mm; NV_Dia=170 mm; PG_Dia=83 mm; PG_Ref=122 mm; PG_depth=14 mm  [stored 0.0459318 ft]; PG_height=467 mm; PG_height_1=425 mm; PG_ref=135 mm; PR_1=61 mm; P_lenght=101 mm; Pilot_Dia_1=46 mm; Pilot_Dia_2=92 mm; Pilot_Dia_3=31 mm  [stored 0.101706 ft]; Pilot_Dia_4=15 mm  [stored 0.0492126 ft]; Pilot_Dia_5=10 mm  [stored 0.0328084 ft]; Pilot_top_1=481 mm; Pilot_top_ref=101 mm; Profile1_Height=292 mm; Profile1_Length=53 mm; Profile1_Length_2=36 mm; Profile_Dia=10 mm  [stored 0.0328084 ft]; Profile_Dia_2=10 mm  [stored 0.0328084 ft]; Profile_Dia_3=20 mm  [stored 0.0656168 ft]; Profile_Dia_Ref=5 mm  [stored 0.0164042 ft]; Profile_Dia_Ref_2=20 mm  [stored 0.0656168 ft]; Profile_height ref=30 mm  [stored 0.0984252 ft]; T_Height=271 mm; T_Height_2=232 mm; T_Height_Ref_1=39 mm  [stored 0.127953 ft]; T_Height_Ref_2=45 mm; T_ref=444 mm; Top_Profile=337 mm; Top_Profile_Ref=342 mm; W=765 mm; W_Ref=751 mm
- 879-0250-00-14400309999_DN250_PN16: Body_Collar_Dia=66 mm; Body_Collar_Dia_2=46 mm; Body_Flange_Dia=209 mm; Body_Flange_Dia_2=228 mm; Body_Height_1=183 mm; Body_Height_2=91 mm; Body_Height_3=105 mm; Body_Height_4=106 mm; Body_Top_Dia=27 mm  [stored 0.0885827 ft]; Body_Top_Dia_2=23 mm; Body_With_Dia=91 mm; Body_With_Dia_1=183 mm; Body_With_Dia_2=183 mm; Bolt_support=562 mm; Bolt_support_2=281 mm; Bolt_support_Dia=20 mm  [stored 0.0656168 ft]; Bolt_support_lenght=145 mm; Bolt_support_lenght_2=155 mm; Bottom_profile=63 mm; D1=160 mm; D3=203 mm; DN=251 mm; Fillet_Length=10 mm  [stored 0.0328084 ft]; Fillet_Length_Ref=30 mm  [stored 0.0984252 ft]; Flange_thickness=22 mm  [stored 0.0721785 ft]; H=800 mm; H3_Ref=790 mm; ID=125 mm; L=730 mm; L_Ref=343 mm; NV_Dia=170 mm; PG_Dia=84 mm; PG_Ref=122 mm; PG_depth=14 mm  [stored 0.0459318 ft]; PG_height=468 mm; PG_height_1=426 mm; PG_ref=135 mm; PR_1=59 mm; P_lenght=101 mm; Pilot_Dia_1=46 mm; Pilot_Dia_2=92 mm; Pilot_Dia_3=31 mm  [stored 0.101706 ft]; Pilot_Dia_4=15 mm  [stored 0.0492126 ft]; Pilot_Dia_5=10 mm  [stored 0.0328084 ft]; Pilot_top_1=490 mm; Pilot_top_ref=87 mm; Profile1_Height=295 mm; Profile1_Length=55 mm; Profile1_Length_2=36 mm; Profile_Dia=10 mm  [stored 0.0328084 ft]; Profile_Dia_2=10 mm  [stored 0.0328084 ft]; Profile_Dia_3=20 mm  [stored 0.0656168 ft]; Profile_Dia_Ref=5 mm  [stored 0.0164042 ft]; Profile_Dia_Ref_2=20 mm  [stored 0.0656168 ft]; Profile_height ref=30 mm  [stored 0.0984252 ft]; T_Height=263 mm; T_Height_2=225 mm; T_Height_Ref_1=38 mm; T_Height_Ref_2=44 mm; T_ref=444 mm; Top_Profile=337 mm; Top_Profile_Ref=342 mm; W=765 mm; W_Ref=751 mm
- 879-0250-00-14400319999_DN250_PN16: Body_Collar_Dia=66 mm; Body_Collar_Dia_2=46 mm; Body_Flange_Dia=209 mm; Body_Flange_Dia_2=228 mm; Body_Height_1=183 mm; Body_Height_2=91 mm; Body_Height_3=81 mm; Body_Height_4=106 mm; Body_Top_Dia=27 mm  [stored 0.0885827 ft]; Body_Top_Dia_2=23 mm; Body_With_Dia=91 mm; Body_With_Dia_1=183 mm; Body_With_Dia_2=183 mm; Bolt_support=562 mm; Bolt_support_2=281 mm; Bolt_support_Dia=20 mm  [stored 0.0656168 ft]; Bolt_support_lenght=145 mm; Bolt_support_lenght_2=155 mm; Bottom_profile=63 mm; D1=160 mm; D3=203 mm; DN=251 mm; Fillet_Length=10 mm  [stored 0.0328084 ft]; Fillet_Length_Ref=30 mm  [stored 0.0984252 ft]; Flange_thickness=22 mm  [stored 0.0721785 ft]; H=800 mm; H3_Ref=790 mm; ID=125 mm; L=730 mm; L_Ref=343 mm; NV_Dia=170 mm; PG_Dia=84 mm; PG_Ref=122 mm; PG_depth=14 mm  [stored 0.0459318 ft]; PG_height=472 mm; PG_height_1=430 mm; PG_ref=135 mm; PR_1=58 mm; P_lenght=103 mm; Pilot_Dia_1=47 mm; Pilot_Dia_2=94 mm; Pilot_Dia_3=31 mm  [stored 0.101706 ft]; Pilot_Dia_4=16 mm  [stored 0.0524934 ft]; Pilot_Dia_5=10 mm  [stored 0.0328084 ft]; Pilot_top_1=479 mm; Pilot_top_ref=99 mm; Profile1_Height=300 mm; Profile1_Length=55 mm; Profile1_Length_2=36 mm; Profile_Dia=10 mm  [stored 0.0328084 ft]; Profile_Dia_2=10 mm  [stored 0.0328084 ft]; Profile_Dia_3=20 mm  [stored 0.0656168 ft]; Profile_Dia_Ref=5 mm  [stored 0.0164042 ft]; Profile_Dia_Ref_2=20 mm  [stored 0.0656168 ft]; Profile_height ref=30 mm  [stored 0.0984252 ft]; T_Height=258 mm; T_Height_2=221 mm; T_Height_Ref_1=37 mm; T_Height_Ref_2=43 mm  [stored 0.141076 ft]; T_ref=446 mm; Top_Profile=337 mm; Top_Profile_Ref=342 mm; W=765 mm; W_Ref=751 mm
- 879-0250-00-144003199A0_DN250_PN16: Body_Collar_Dia=66 mm; Body_Collar_Dia_2=46 mm; Body_Flange_Dia=209 mm; Body_Flange_Dia_2=228 mm; Body_Height_1=183 mm; Body_Height_2=91 mm; Body_Height_3=81 mm; Body_Height_4=106 mm; Body_Top_Dia=27 mm  [stored 0.0885827 ft]; Body_Top_Dia_2=23 mm; Body_With_Dia=91 mm; Body_With_Dia_1=183 mm; Body_With_Dia_2=183 mm; Bolt_support=562 mm; Bolt_support_2=281 mm; Bolt_support_Dia=20 mm  [stored 0.0656168 ft]; Bolt_support_lenght=145 mm; Bolt_support_lenght_2=155 mm; Bottom_profile=63 mm; D1=160 mm; D3=203 mm; DN=251 mm; Fillet_Length=10 mm  [stored 0.0328084 ft]; Fillet_Length_Ref=30 mm  [stored 0.0984252 ft]; Flange_thickness=22 mm  [stored 0.0721785 ft]; H=806 mm; H3_Ref=796 mm; ID=125 mm; L=730 mm; L_Ref=343 mm; NV_Dia=170 mm; PG_Dia=84 mm; PG_Ref=122 mm; PG_depth=14 mm  [stored 0.0459318 ft]; PG_height=485 mm; PG_height_1=443 mm; PG_ref=135 mm; PR_1=56 mm; P_lenght=103 mm; Pilot_Dia_1=47 mm; Pilot_Dia_2=94 mm; Pilot_Dia_3=31 mm  [stored 0.101706 ft]; Pilot_Dia_4=16 mm  [stored 0.0524934 ft]; Pilot_Dia_5=10 mm  [stored 0.0328084 ft]; Pilot_top_1=482 mm; Pilot_top_ref=102 mm; Profile1_Height=315 mm; Profile1_Length=55 mm; Profile1_Length_2=36 mm; Profile_Dia=10 mm  [stored 0.0328084 ft]; Profile_Dia_2=10 mm  [stored 0.0328084 ft]; Profile_Dia_3=20 mm  [stored 0.0656168 ft]; Profile_Dia_Ref=5 mm  [stored 0.0164042 ft]; Profile_Dia_Ref_2=20 mm  [stored 0.0656168 ft]; Profile_height ref=30 mm  [stored 0.0984252 ft]; T_Height=249 mm; T_Height_2=213 mm; T_Height_Ref_1=36 mm; T_Height_Ref_2=41 mm  [stored 0.134514 ft]; T_ref=457 mm; Top_Profile=337 mm; Top_Profile_Ref=342 mm; W=765 mm; W_Ref=751 mm
- 879-0250-00-14400329999_DN250_PN16: Body_Collar_Dia=66 mm; Body_Collar_Dia_2=46 mm; Body_Flange_Dia=209 mm; Body_Flange_Dia_2=228 mm; Body_Height_1=183 mm; Body_Height_2=91 mm; Body_Height_3=81 mm; Body_Height_4=106 mm; Body_Top_Dia=27 mm  [stored 0.0885827 ft]; Body_Top_Dia_2=23 mm; Body_With_Dia=91 mm; Body_With_Dia_1=183 mm; Body_With_Dia_2=183 mm; Bolt_support=562 mm; Bolt_support_2=281 mm; Bolt_support_Dia=20 mm  [stored 0.0656168 ft]; Bolt_support_lenght=145 mm; Bolt_support_lenght_2=155 mm; Bottom_profile=63 mm; D1=160 mm; D3=203 mm; DN=251 mm; Fillet_Length=10 mm  [stored 0.0328084 ft]; Fillet_Length_Ref=30 mm  [stored 0.0984252 ft]; Flange_thickness=22 mm  [stored 0.0721785 ft]; H=800 mm; H3_Ref=790 mm; ID=125 mm; L=730 mm; L_Ref=343 mm; NV_Dia=170 mm; PG_Dia=84 mm; PG_Ref=122 mm; PG_depth=14 mm  [stored 0.0459318 ft]; PG_height=466 mm; PG_height_1=424 mm; PG_ref=135 mm; PR_1=60 mm; P_lenght=101 mm; Pilot_Dia_1=46 mm; Pilot_Dia_2=92 mm; Pilot_Dia_3=31 mm  [stored 0.101706 ft]; Pilot_Dia_4=15 mm  [stored 0.0492126 ft]; Pilot_Dia_5=10 mm  [stored 0.0328084 ft]; Pilot_top_1=479 mm; Pilot_top_ref=99 mm; Profile1_Height=292 mm; Profile1_Length=55 mm; Profile1_Length_2=36 mm; Profile_Dia=10 mm  [stored 0.0328084 ft]; Profile_Dia_2=10 mm  [stored 0.0328084 ft]; Profile_Dia_3=20 mm  [stored 0.0656168 ft]; Profile_Dia_Ref=5 mm  [stored 0.0164042 ft]; Profile_Dia_Ref_2=20 mm  [stored 0.0656168 ft]; Profile_height ref=30 mm  [stored 0.0984252 ft]; T_Height=266 mm; T_Height_2=228 mm; T_Height_Ref_1=38 mm; T_Height_Ref_2=44 mm; T_ref=442 mm; Top_Profile=337 mm; Top_Profile_Ref=342 mm; W=765 mm; W_Ref=751 mm
- 879-0250-00-14400339999_DN250_PN16: Body_Collar_Dia=66 mm; Body_Collar_Dia_2=46 mm; Body_Flange_Dia=209 mm; Body_Flange_Dia_2=228 mm; Body_Height_1=183 mm; Body_Height_2=91 mm; Body_Height_3=105 mm; Body_Height_4=106 mm; Body_Top_Dia=27 mm  [stored 0.0885827 ft]; Body_Top_Dia_2=23 mm; Body_With_Dia=91 mm; Body_With_Dia_1=183 mm; Body_With_Dia_2=183 mm; Bolt_support=562 mm; Bolt_support_2=281 mm; Bolt_support_Dia=20 mm  [stored 0.0656168 ft]; Bolt_support_lenght=145 mm; Bolt_support_lenght_2=155 mm; Bottom_profile=63 mm; D1=160 mm; D3=203 mm; DN=251 mm; Fillet_Length=10 mm  [stored 0.0328084 ft]; Fillet_Length_Ref=30 mm  [stored 0.0984252 ft]; Flange_thickness=22 mm  [stored 0.0721785 ft]; H=800 mm; H3_Ref=790 mm; ID=125 mm; L=730 mm; L_Ref=343 mm; NV_Dia=170 mm; PG_Dia=84 mm; PG_Ref=122 mm; PG_depth=14 mm  [stored 0.0459318 ft]; PG_height=468 mm; PG_height_1=426 mm; PG_ref=135 mm; PR_1=59 mm; P_lenght=101 mm; Pilot_Dia_1=46 mm; Pilot_Dia_2=92 mm; Pilot_Dia_3=31 mm  [stored 0.101706 ft]; Pilot_Dia_4=15 mm  [stored 0.0492126 ft]; Pilot_Dia_5=10 mm  [stored 0.0328084 ft]; Pilot_top_1=490 mm; Pilot_top_ref=87 mm; Profile1_Height=295 mm; Profile1_Length=55 mm; Profile1_Length_2=36 mm; Profile_Dia=10 mm  [stored 0.0328084 ft]; Profile_Dia_2=10 mm  [stored 0.0328084 ft]; Profile_Dia_3=20 mm  [stored 0.0656168 ft]; Profile_Dia_Ref=5 mm  [stored 0.0164042 ft]; Profile_Dia_Ref_2=20 mm  [stored 0.0656168 ft]; Profile_height ref=30 mm  [stored 0.0984252 ft]; T_Height=263 mm; T_Height_2=225 mm; T_Height_Ref_1=38 mm; T_Height_Ref_2=44 mm; T_ref=444 mm; Top_Profile=337 mm; Top_Profile_Ref=342 mm; W=765 mm; W_Ref=751 mm

note: [stored X ft] marks values corroborated as IEEE doubles in the binary element streams (Revit-internal decimal feet)

## geometry (parser evidence)
native form markers: Sweep x4
no freeform markers — native parametric forms only
